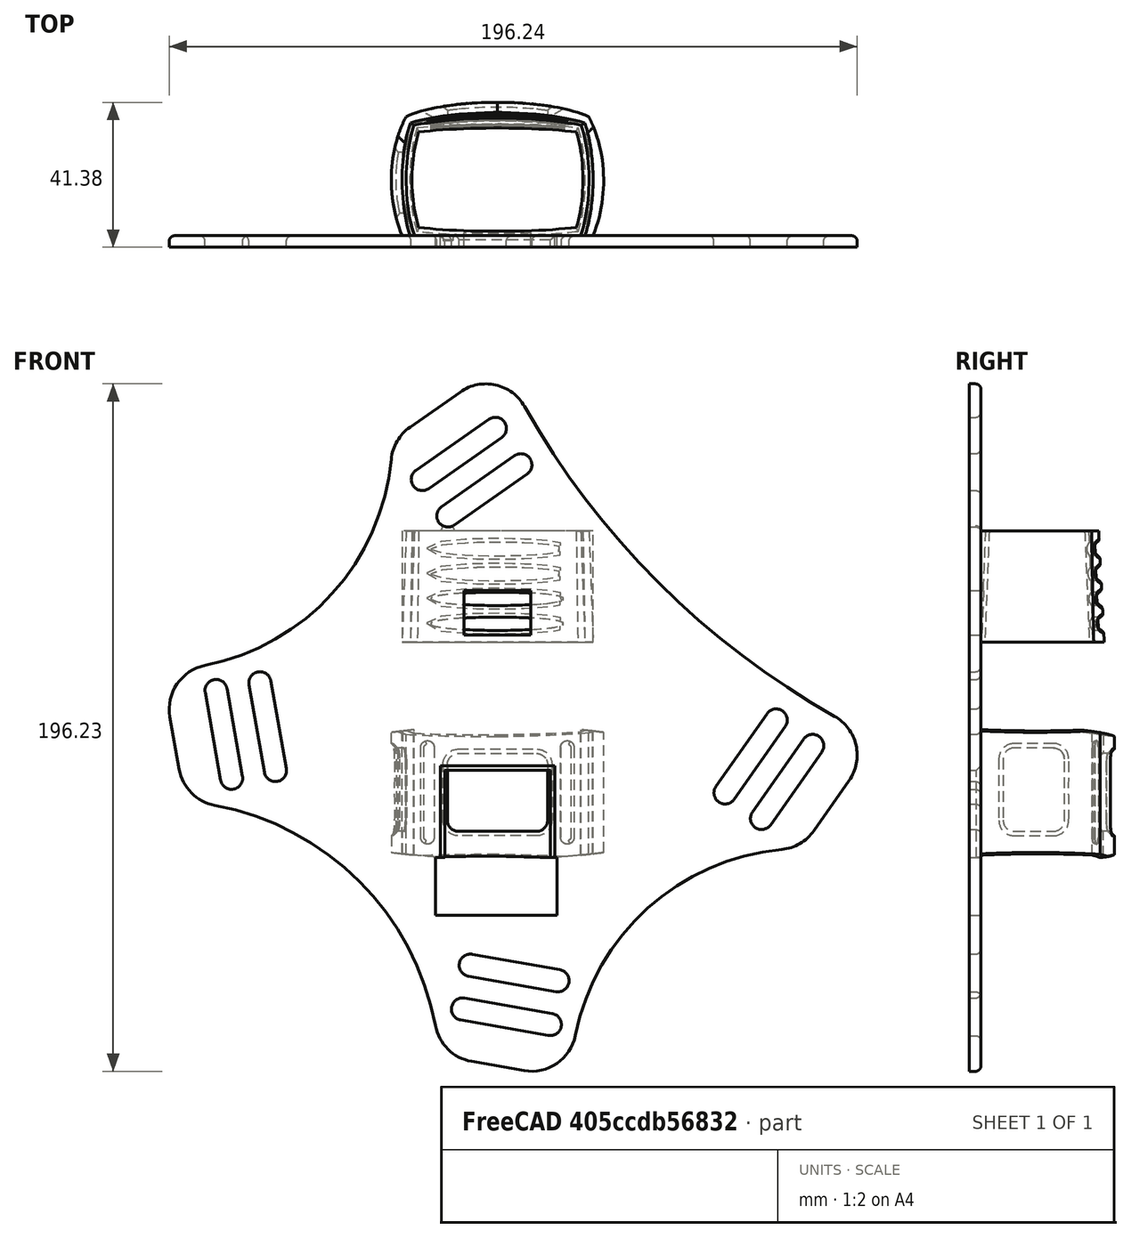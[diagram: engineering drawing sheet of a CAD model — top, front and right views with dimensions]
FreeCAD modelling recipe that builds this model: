
FCSTD DOCUMENT  (FreeCAD 0.20R29177 (Git))
Label: v2_1
License: All rights reserved
LicenseURL: http://en.wikipedia.org/wiki/All_rights_reserved
objects: Sketcher::SketchObject×23, PartDesign::Pocket×11, PartDesign::Pad×6, PartDesign::Fillet×3, PartDesign::Plane×2, PartDesign::SubtractiveLoft×2, PartDesign::Chamfer×1, PartDesign::Body×1
note: 72 computed .brp shape members not serialized (recipe doc carries the construction recipe); baked Part::Feature solids carry a one-line shape summary decoded from their .brp

FEATURE [Sketcher::SketchObject] Sketch
  FullyConstrained = false
  MapMode = 5
  Support = -> [XY_Plane]
  sketch-geometry (33):
    g0: ArcOfEllipse CenterX=0 CenterY=14.8987 CenterZ=0 NormalX=0 NormalY=0 NormalZ=1 MajorRadius=33.1985 MinorRadius=27.0767 AngleXU=-1.48295 StartAngle=4.10821 EndAngle=5.10673
    g1: ArcOfEllipse CenterX=0 CenterY=14.8987 CenterZ=0 NormalX=0 NormalY=0 NormalZ=1 MajorRadius=33.1985 MinorRadius=27.0767 AngleXU=-1.64554 StartAngle=1.16593 EndAngle=2.16406
    g2: ArcOfEllipse CenterX=0.00426746 CenterY=30.0382 CenterZ=0 NormalX=0 NormalY=0 NormalZ=1 MajorRadius=25.3994 MinorRadius=4.86502 AngleXU=3.14061 StartAngle=3.50205 EndAngle=5.93299
    g3: LineSegment StartX=-23.7833 StartY=0 StartZ=0 EndX=23.8417 EndY=0 EndZ=0
    g4: LineSegment StartX=-23.8519 StartY=31.7308 StartZ=0 EndX=23.7731 EndY=31.7308 EndZ=0
    g5: GeomPoint X=-26.9875 Y=12.7 Z=0
    g6: LineSegment StartX=-26.9875 StartY=12.7 StartZ=0 EndX=26.9875 EndY=12.7 EndZ=0
    g7: LineSegment StartX=0 StartY=0 StartZ=0 EndX=26.9875 EndY=12.7 EndZ=0
    g8: LineSegment StartX=0 StartY=0 StartZ=0 EndX=-26.9875 EndY=12.7 EndZ=0
    g9: LineSegment StartX=-26.9875 StartY=0 StartZ=0 EndX=-26.9875 EndY=12.7 EndZ=0
    g10: ArcOfEllipse CenterX=0.00426746 CenterY=30.0382 CenterZ=0 NormalX=0 NormalY=0 NormalZ=1 MajorRadius=29.8873 MinorRadius=8.04002 AngleXU=3.14073 StartAngle=3.65661 EndAngle=5.7746
    g11: LineSegment StartX=23.7731 StartY=31.7308 StartZ=0 EndX=26.0182 EndY=33.9758 EndZ=0
    g12: LineSegment StartX=-23.8519 StartY=31.7308 StartZ=0 EndX=-26.097 EndY=33.9758 EndZ=0
    g13: GeomPoint X=0 Y=34.9033 Z=0
    g14: LineSegment StartX=0 StartY=34.9033 StartZ=0 EndX=0 EndY=38.0783 EndZ=0
    g15: LineSegment StartX=26.9875 StartY=12.7 StartZ=0 EndX=30.1526 EndY=12.4491 EndZ=0
    g16: GeomPoint X=26.9875 Y=12.7 Z=0
    g17: LineSegment StartX=23.8417 StartY=0 StartZ=0 EndX=26.7524 EndY=-1.26846 EndZ=0
    g18: GeomPoint X=23.8417 Y=6e-16 Z=0
    g19: ArcOfEllipse CenterX=2.35624 CenterY=14.2309 CenterZ=0 NormalX=0 NormalY=0 NormalZ=1 MajorRadius=34.768 MinorRadius=27.8462 AngleXU=1.46882 StartAngle=4.37163 EndAngle=5.39941
    g20: LineSegment StartX=-26.9875 StartY=12.7 StartZ=0 EndX=-30.1514 EndY=12.4352 EndZ=0
    g21: LineSegment StartX=-23.7833 StartY=0 StartZ=0 EndX=-26.6887 EndY=-1.28025 EndZ=0
    g22: GeomPoint X=-23.7833 Y=-5.07e-13 Z=0
    g23: GeomPoint X=-26.9875 Y=12.7 Z=0
    g24: ArcOfEllipse CenterX=-2.35136 CenterY=14.2309 CenterZ=0 NormalX=0 NormalY=0 NormalZ=1 MajorRadius=34.768 MinorRadius=27.8462 AngleXU=1.68398 StartAngle=0.874461 EndAngle=1.90273
    g25: GeomPoint X=0 Y=-6.45413 Z=0
    g26: LineSegment StartX=2.35624 StartY=14.2309 StartZ=0 EndX=-2.35136 EndY=14.2309 EndZ=0
    g27: GeomPoint X=27.2821 Y=0 Z=0
    g28: GeomPoint X=-27.2294 Y=0 Z=0
    g29: LineSegment StartX=27.2821 StartY=0 StartZ=0 EndX=27.2821 EndY=-3.175 EndZ=0
    g30: LineSegment StartX=27.2821 StartY=-3.175 StartZ=0 EndX=-27.2294 EndY=-3.175 EndZ=0
    g31: LineSegment StartX=-27.2294 StartY=-3.175 StartZ=0 EndX=-27.2294 EndY=0 EndZ=0
    g32: LineSegment StartX=-23.7833 StartY=0 StartZ=0 EndX=23.8417 EndY=0 EndZ=0
  constraints (91):
    c: PointOnObject(g0,g-1)
    c: PointOnObject(g1,g-1)
    c: DistanceX(g0,g1) = 47.625
    c: Coincident(g1,g2)
    c: Coincident(g3,g0)
    c: Coincident(g3,g1)
    c: Block(g2)
    c: Coincident(g0,g2)
    c: Coincident(g4,g0)
    c: Coincident(g4,g1)
    c: Horizontal(g4)
    c: DistanceX(g4,g4) = 47.625
    c: PointOnObject(g5,g0)
    c: Coincident(g6,g5)
    c: Horizontal(g6)
    c: DistanceX(g6,g6) = 53.975
    c: PointOnObject(g6,g1)
    c: Coincident(g7,g-1)
    c: Coincident(g7,g6)
    c: Coincident(g8,g7)
    c: Coincident(g8,g5)
    c: Equal(g0,g1)
    c: PointOnObject(g9,g-1)
    c: Vertical(g9)
    c: Coincident(g9,g5)
    c: DistanceY(g9,g9) = 12.7
    c: Equal(g8,g7)
    c: PointOnObject(g1,g-2)
    c: Coincident(g0,g1)
    c: Coincident(g10,g2)
    c: Coincident(g11,g1)
    c: Coincident(g12,g0)
    c: Angle(g11) = 0.785398
    c: Perpendicular(g12,g11)
    c: Distance(g11) = 3.175
    c: Equal(g12,g11)
    c: Coincident(g10,g11)
    c: PointOnObject(g13,g2)
    c: PointOnObject(g13,g-2)
    c: Coincident(g14,g13)
    c: PointOnObject(g14,g10)
    c: PointOnObject(g14,g-2)
    c: DistanceY(g14,g14) = 3.175
    c: Coincident(g10,g12)
    c: Coincident(g15,g6)
    c: PointOnObject(g16,g1)
    c: PointOnObject(g16,g15)
    c: Perpendicular(g1,g15,g16) = 4.71239
    c: Distance(g15) = 3.175
    c: Coincident(g17,g1)
    c: PointOnObject(g18,g1)
    c: PointOnObject(g18,g17)
    c: Perpendicular(g1,g17,g18) = 4.71239
    c: Distance(g17) = 3.175
    c: Coincident(g19,g10)
    c: Coincident(g20,g5)
    c: Coincident(g21,g0)
    c: PointOnObject(g22,g0)
    c: PointOnObject(g22,g21)
    c: Perpendicular(g0,g21,g22) = 4.71239
    c: PointOnObject(g23,g0)
    c: PointOnObject(g23,g20)
    c: Perpendicular(g0,g20,g23) = 4.71239
    c: Equal(g20,g21)
    c: Equal(g21,g17)
    c: InternalAlignment(g25,g24)
    c: PointOnObject(g20,g24)
    c: Coincident(g24,g10)
    c: PointOnObject(g15,g19)
    c: Equal(g19,g24)
    c: Coincident(g26,g19)
    c: Coincident(g26,g24)
    c: Horizontal(g26)
    c: PointOnObject(g25,g-2)
    c: PointOnObject(g27,g-1)
    c: PointOnObject(g27,g19)
    c: PointOnObject(g28,g24)
    c: PointOnObject(g28,g-1)
    c: Coincident(g29,g30)
    c: Coincident(g30,g31)
    c: Horizontal(g30)
    c: Vertical(g29)
    c: Vertical(g31)
    c: PointOnObject(g27,g29)
    c: DistanceY(g29,g29) = 3.175
    c: PointOnObject(g24,g31)
    c: PointOnObject(g19,g29)
    c: Block(g24)
    c: Coincident(g32,g0)
    c: PointOnObject(g32,g17)
    c: Horizontal(g32)
FEATURE [PartDesign::Pad] Pad
  Direction = (0,0,1)
  Length = 38.1
  Length2 = 9.906
  Profile = -> Sketch
  ReferenceAxis = -> Sketch [N_Axis]
  Type = 0
FEATURE [Sketcher::SketchObject] Sketch001
  FullyConstrained = true
  MapMode = 5
  Placement = pos=(0,0,0) rot=(1,0,0;1.5708rad)
  Support = -> [XZ_Plane]
FEATURE [PartDesign::Plane] DatumPlane
  AttachmentOffset = pos=(25.4,25.4,50.8) rot=(0,0,1;0rad)
  Length = 235.383
  MapMode = 5
  Placement = pos=(-25.4,50.8,25.4) rot=(0,0.707107,0.707107;3.14159rad)
  ResizeMode = 0
  Support = -> [Pad]
  Width = 235.383
FEATURE [Sketcher::SketchObject] Sketch002
  ExternalGeometry = -> [Pad]
  FullyConstrained = true
  MapMode = 5
  Placement = pos=(-25.4,50.8,25.4) rot=(0,0.707107,0.707107;3.14159rad)
  Support = -> [DatumPlane]
  sketch-geometry (15):
    g0: LineSegment StartX=-36.5168 StartY=4.7625 StartZ=0 EndX=-14.2918 EndY=4.7625 EndZ=0
    g1: LineSegment StartX=-11.1168 StartY=1.5875 StartZ=0 EndX=-11.1168 EndY=-14.2875 EndZ=0
    g2: LineSegment StartX=-14.2918 StartY=-17.4625 StartZ=0 EndX=-36.5168 EndY=-17.4625 EndZ=0
    g3: LineSegment StartX=-39.6918 StartY=-14.2875 StartZ=0 EndX=-39.6918 EndY=1.5875 EndZ=0
    g4: LineSegment StartX=-55.2916 StartY=-25.4 StartZ=0 EndX=-39.6918 EndY=-17.4625 EndZ=0
    g5: LineSegment StartX=4.48307 StartY=-25.4 StartZ=0 EndX=-11.1168 EndY=-17.4625 EndZ=0
    g6: LineSegment StartX=4.48307 StartY=12.7 StartZ=0 EndX=-11.1168 EndY=4.7625 EndZ=0
    g7: ArcOfCircle CenterX=-36.5168 CenterY=1.5875 CenterZ=0 NormalX=0 NormalY=0 NormalZ=1 AngleXU=0 Radius=3.175 StartAngle=1.5708 EndAngle=3.14159
    g8: GeomPoint X=-39.6918 Y=4.7625 Z=0
    g9: ArcOfCircle CenterX=-36.5168 CenterY=-14.2875 CenterZ=0 NormalX=0 NormalY=0 NormalZ=1 AngleXU=0 Radius=3.175 StartAngle=3.14159 EndAngle=4.71239
    g10: GeomPoint X=-39.6918 Y=-17.4625 Z=0
    g11: ArcOfCircle CenterX=-14.2918 CenterY=-14.2875 CenterZ=0 NormalX=0 NormalY=0 NormalZ=1 AngleXU=0 Radius=3.175 StartAngle=4.71239 EndAngle=6.28319
    g12: GeomPoint X=-11.1168 Y=-17.4625 Z=0
    g13: ArcOfCircle CenterX=-14.2918 CenterY=1.5875 CenterZ=0 NormalX=0 NormalY=0 NormalZ=1 AngleXU=0 Radius=3.175 StartAngle=2.52e-14 EndAngle=1.5708
    g14: GeomPoint X=-11.1168 Y=4.7625 Z=0
  constraints (34):
    c: Horizontal(g0)
    c: Horizontal(g2)
    c: Vertical(g1)
    c: Vertical(g3)
    c: DistanceX(g8,g14) = 28.575
    c: DistanceY(g12,g14) = 22.225
    c: Coincident(g4,g-3)
    c: Coincident(g4,g10)
    c: Coincident(g5,g-3)
    c: Coincident(g5,g12)
    c: Coincident(g6,g-4)
    c: Coincident(g6,g14)
    c: Equal(g6,g5)
    c: Equal(g5,g4)
    c: PointOnObject(g8,g0)
    c: PointOnObject(g8,g3)
    c: Tangent(g0,g7) = 1.5708
    c: Tangent(g3,g7) = 1.5708
    c: PointOnObject(g10,g2)
    c: PointOnObject(g10,g3)
    c: Tangent(g2,g9) = 1.5708
    c: Tangent(g3,g9) = 1.5708
    c: PointOnObject(g12,g2)
    c: PointOnObject(g12,g1)
    c: Tangent(g2,g11) = 1.5708
    c: Tangent(g1,g11) = 1.5708
    c: PointOnObject(g14,g1)
    c: PointOnObject(g14,g0)
    c: Tangent(g1,g13) = 1.5708
    c: Tangent(g0,g13) = 1.5708
    c: Equal(g7,g9)
    c: Equal(g9,g11)
    c: Equal(g11,g13)
    c: Radius(g13) = 3.175
FEATURE [PartDesign::Pocket] Pocket
  BaseFeature = -> Pad
  Direction = (0,-1,2e-16)
  Length = 0
  Length2 = 5.08
  Profile = -> Sketch002
  ReferenceAxis = -> Sketch002 [N_Axis]
  Type = 3
  UpToFace = -> Pad [Face8]
FEATURE [Sketcher::SketchObject] Sketch003
  FullyConstrained = true
  MapMode = 5
  Placement = pos=(-25.4,50.8,25.4) rot=(0,0.707107,0.707107;3.14159rad)
  Support = -> [DatumPlane]
FEATURE [Sketcher::SketchObject] Sketch004
  ExternalGeometry = -> [Pocket]
  FullyConstrained = true
  MapMode = 5
  Placement = pos=(0,0,0) rot=(0.57735,0.57735,0.57735;2.0944rad)
  Support = -> [YZ_Plane]
  sketch-geometry (17):
    g0: LineSegment StartX=9.525 StartY=31.75 StartZ=0 EndX=20.6375 EndY=31.75 EndZ=0
    g1: LineSegment StartX=23.8125 StartY=28.575 StartZ=0 EndX=23.8125 EndY=11.1125 EndZ=0
    g2: LineSegment StartX=20.6375 StartY=7.9375 StartZ=0 EndX=9.525 EndY=7.9375 EndZ=0
    g3: LineSegment StartX=6.35 StartY=11.1125 StartZ=0 EndX=6.35 EndY=28.575 EndZ=0
    g4: ArcOfCircle CenterX=9.525 CenterY=28.575 CenterZ=0 NormalX=0 NormalY=0 NormalZ=1 AngleXU=0 Radius=3.175 StartAngle=1.5708 EndAngle=3.14159
    g5: GeomPoint X=6.35 Y=31.75 Z=0
    g6: ArcOfCircle CenterX=20.6375 CenterY=28.575 CenterZ=0 NormalX=0 NormalY=0 NormalZ=1 AngleXU=0 Radius=3.175 StartAngle=2e-16 EndAngle=1.5708
    g7: GeomPoint X=23.8125 Y=31.75 Z=0
    g8: ArcOfCircle CenterX=20.6375 CenterY=11.1125 CenterZ=0 NormalX=0 NormalY=0 NormalZ=1 AngleXU=0 Radius=3.175 StartAngle=4.71239 EndAngle=6.28319
    g9: GeomPoint X=23.8125 Y=7.9375 Z=0
    g10: ArcOfCircle CenterX=9.525 CenterY=11.1125 CenterZ=0 NormalX=0 NormalY=0 NormalZ=1 AngleXU=0 Radius=3.175 StartAngle=3.14159 EndAngle=4.71239
    g11: GeomPoint X=6.35 Y=7.9375 Z=0
    g12: LineSegment StartX=6.35 StartY=28.575 StartZ=0 EndX=23.8125 EndY=28.575 EndZ=0
    g13: LineSegment StartX=9.525 StartY=31.75 StartZ=0 EndX=9.525 EndY=7.9375 EndZ=0
    g14: LineSegment StartX=6.35 StartY=28.575 StartZ=0 EndX=-3.175 EndY=28.575 EndZ=0
    g15: LineSegment StartX=-3.175 StartY=38.1 StartZ=0 EndX=31.7308 EndY=38.1 EndZ=0
    g16: LineSegment StartX=9.525 StartY=31.75 StartZ=0 EndX=9.525 EndY=38.1 EndZ=0
  constraints (40):
    c: Horizontal(g0)
    c: Horizontal(g2)
    c: Vertical(g1)
    c: Vertical(g3)
    c: PointOnObject(g5,g0)
    c: PointOnObject(g5,g3)
    c: Tangent(g0,g4) = 1.5708
    c: Tangent(g3,g4) = 1.5708
    c: PointOnObject(g7,g0)
    c: PointOnObject(g7,g1)
    c: Tangent(g0,g6) = 1.5708
    c: Tangent(g1,g6) = 1.5708
    c: PointOnObject(g9,g1)
    c: PointOnObject(g9,g2)
    c: Tangent(g1,g8) = 1.5708
    c: Tangent(g2,g8) = 1.5708
    c: PointOnObject(g11,g2)
    c: PointOnObject(g11,g3)
    c: Tangent(g2,g10) = 1.5708
    c: Tangent(g3,g10) = 1.5708
    c: Equal(g4,g6)
    c: Equal(g6,g8)
    c: Equal(g8,g10)
    c: Radius(g10) = 3.175
    c: Coincident(g12,g3)
    c: DistanceX(g12,g12) = 17.4625
    c: Coincident(g12,g1)
    c: Coincident(g13,g0)
    c: Coincident(g13,g2)
    c: DistanceY(g13,g13) = 23.8125
    c: Coincident(g14,g3)
    c: PointOnObject(g14,g-3)
    c: Horizontal(g14)
    c: DistanceX(g14,g14) = 9.525
    c: Coincident(g15,g-3)
    c: Coincident(g15,g-4)
    c: Coincident(g16,g0)
    c: PointOnObject(g16,g15)
    c: Vertical(g16)
    c: DistanceY(g16,g16) = 6.35
FEATURE [PartDesign::Pocket] Pocket001
  BaseFeature = -> Pocket
  Direction = (-1,2e-16,-3e-16)
  Length = 5.08
  Length2 = 5.08
  Profile = -> Sketch004
  ReferenceAxis = -> Sketch004 [N_Axis]
  Type = 1
FEATURE [Sketcher::SketchObject] Sketch005
  ExternalGeometry = -> [Pocket001]
  FullyConstrained = true
  MapMode = 5
  Placement = pos=(-25.4,50.8,25.4) rot=(0,0.707107,0.707107;3.14159rad)
  Support = -> [DatumPlane]
  sketch-geometry (11):
    g0: Ellipse CenterX=-25.4043 CenterY=-6.35 CenterZ=0 NormalX=0 NormalY=0 NormalZ=1 MajorRadius=69.5483 MinorRadius=19.05 AngleXU=-1e-16
    g1: LineSegment StartX=44.144 StartY=-6.35 StartZ=0 EndX=-94.9526 EndY=-6.35 EndZ=0
    g2: LineSegment StartX=-25.4043 StartY=12.7 StartZ=0 EndX=-25.4043 EndY=-25.4 EndZ=0
    g3: GeomPoint X=41.4842 Y=-6.35 Z=0
    g4: GeomPoint X=-92.2927 Y=-6.35 Z=0
    g5: LineSegment StartX=-55.2916 StartY=12.7 StartZ=0 EndX=-25.4043 EndY=-6.35 EndZ=0
    g6: LineSegment StartX=-25.4043 StartY=-6.35 StartZ=0 EndX=4.48307 EndY=12.7 EndZ=0
    g7: LineSegment StartX=-111.897 StartY=37.229 StartZ=0 EndX=59.9655 EndY=37.229 EndZ=0
    g8: LineSegment StartX=59.9655 StartY=37.229 StartZ=0 EndX=59.9655 EndY=-34.3386 EndZ=0
    g9: LineSegment StartX=59.9655 StartY=-34.3386 StartZ=0 EndX=-111.897 EndY=-34.3386 EndZ=0
    g10: LineSegment StartX=-111.897 StartY=-34.3386 StartZ=0 EndX=-111.897 EndY=37.229 EndZ=0
  constraints (20):
    c: InternalAlignment(g1-g4 -> g0) x4
    c: Tangent(g0,g-3)
    c: Vertical(g2)
    c: PointOnObject(g2,g-4)
    c: Coincident(g5,g-3)
    c: Coincident(g5,g0)
    c: Coincident(g6,g0)
    c: Coincident(g6,g-3)
    c: Equal(g6,g5)
    c: Coincident(g7,g8)
    c: Coincident(g8,g9)
    c: Coincident(g9,g10)
    c: Coincident(g10,g7)
    c: Horizontal(g7)
    c: Horizontal(g9)
    c: Vertical(g8)
    c: Vertical(g10)
    c: Block(g0)
    c: Block(g9)
    c: Block(g7)
FEATURE [PartDesign::Pocket] Pocket002
  BaseFeature = -> Pocket001
  Direction = (0,-1,2e-16)
  Length = 0
  Length2 = 5.08
  Profile = -> Sketch005
  ReferenceAxis = -> Sketch005 [N_Axis]
  Type = 3
  UpToFace = -> Pocket001 [Face16]
FEATURE [Sketcher::SketchObject] Sketch006
  FullyConstrained = true
  MapMode = 5
  Placement = pos=(0,0,0) rot=(0.57735,0.57735,0.57735;2.0944rad)
  Support = -> [YZ_Plane]
  sketch-geometry (7):
    g0: Ellipse CenterX=-43.899 CenterY=18.1751 CenterZ=0 NormalX=0 NormalY=0 NormalZ=1 MajorRadius=123.401 MinorRadius=22.5272 AngleXU=0
    g1: GeomPoint X=77.4281 Y=18.1751 Z=0
    g2: GeomPoint X=-165.226 Y=18.1751 Z=0
    g3: LineSegment StartX=-223.185 StartY=118.003 StartZ=0 EndX=167.895 EndY=118.003 EndZ=0
    g4: LineSegment StartX=167.895 StartY=118.003 StartZ=0 EndX=167.895 EndY=-87.3007 EndZ=0
    g5: LineSegment StartX=167.895 StartY=-87.3007 StartZ=0 EndX=-223.185 EndY=-87.3007 EndZ=0
    g6: LineSegment StartX=-223.185 StartY=-87.3007 StartZ=0 EndX=-223.185 EndY=118.003 EndZ=0
  constraints (13):
    c: InternalAlignment(g1,g0)
    c: InternalAlignment(g2,g0)
    c: Coincident(g3,g4)
    c: Coincident(g4,g5)
    c: Coincident(g5,g6)
    c: Coincident(g6,g3)
    c: Horizontal(g3)
    c: Horizontal(g5)
    c: Vertical(g4)
    c: Vertical(g6)
    c: Block(g0)
    c: Block(g3)
    c: Block(g4)
FEATURE [PartDesign::Pocket] Pocket003
  BaseFeature = -> Pocket002
  Direction = (-1,2e-16,-3e-16)
  Length = 233.68
  Length2 = 157.48
  Profile = -> Sketch006
  ReferenceAxis = -> Sketch006 [N_Axis]
  TaperAngle2 = 1
  Type = 4
FEATURE [Sketcher::SketchObject] Sketch007
  ExternalGeometry = -> [Pocket003]
  FullyConstrained = true
  MapMode = 5
  Placement = pos=(0,-3.175,0) rot=(1,0,0;1.5708rad)
  sketch-geometry (6):
    g0: LineSegment StartX=-15.077 StartY=0 StartZ=0 EndX=15.0855 EndY=0 EndZ=0
    g1: LineSegment StartX=15.0855 StartY=0 StartZ=0 EndX=15.0855 EndY=25.4 EndZ=0
    g2: LineSegment StartX=15.0855 StartY=25.4 StartZ=0 EndX=-15.077 EndY=25.4 EndZ=0
    g3: LineSegment StartX=-15.077 StartY=25.4 StartZ=0 EndX=-15.077 EndY=0 EndZ=0
    g4: LineSegment StartX=-11.1082 StartY=30.1625 StartZ=0 EndX=-15.077 EndY=25.4 EndZ=0
    g5: LineSegment StartX=11.1168 StartY=30.1625 StartZ=0 EndX=15.0855 EndY=25.4 EndZ=0
  constraints (15):
    c: Coincident(g0,g1)
    c: Coincident(g1,g2)
    c: Coincident(g2,g3)
    c: Coincident(g3,g0)
    c: Horizontal(g2)
    c: Vertical(g1)
    c: Vertical(g3)
    c: DistanceX(g2,g2) = 30.1625
    c: Coincident(g4,g2)
    c: Coincident(g5,g1)
    c: Equal(g4,g5)
    c: DistanceY(g1,g1) = 25.4
    c: Tangent(g-1,g0)
    c: Coincident(g5,g-3)
    c: Coincident(g4,g-4)
FEATURE [PartDesign::Pocket] Pocket004
  BaseFeature = -> Pocket003
  Direction = (0,1,-2e-16)
  Length = 5.08
  Length2 = 5.08
  Profile = -> Sketch007
  ReferenceAxis = -> Sketch007 [N_Axis]
  Type = 2
FEATURE [PartDesign::Chamfer] Chamfer
  Angle = 45
  Base = -> Pocket004 [Edge11,Edge89,Edge88,Edge39,Edge87]
  BaseFeature = -> Pocket004
  ChamferType = 0
  FlipDirection = false
  Size = 1.27
  Size2 = 1
  SupportTransform = false
  UseAllEdges = false
FEATURE [PartDesign::Plane] DatumPlane001
  Length = 235.449
  MapMode = 13
  Placement = pos=(3.70843,34.4094,22.7542) rot=(0.000335,0.707107,0.707107;3.14092rad)
  ResizeMode = 0
  Support = -> [Chamfer]
  Width = 235.389
FEATURE [Sketcher::SketchObject] Sketch008
  ExternalGeometry = -> [Chamfer]
  FullyConstrained = true
  MapMode = 5
  Placement = pos=(3.70843,34.4094,22.7542) rot=(0.000335,0.707107,0.707107;3.14092rad)
  Support = -> [DatumPlane001]
  sketch-geometry (14):
    g0: ArcOfCircle CenterX=23.684 CenterY=9.16871 CenterZ=0 NormalX=0 NormalY=0 NormalZ=1 AngleXU=0 Radius=1.905 StartAngle=0 EndAngle=3.14159
    g1: ArcOfCircle CenterX=23.684 CenterY=-16.5768 CenterZ=0 NormalX=0 NormalY=0 NormalZ=1 AngleXU=0 Radius=1.905 StartAngle=3.14159 EndAngle=6.28319
    g2: LineSegment StartX=21.779 StartY=9.16871 StartZ=0 EndX=21.779 EndY=-16.5768 EndZ=0
    g3: LineSegment StartX=25.589 StartY=-16.5768 StartZ=0 EndX=25.589 EndY=9.16871 EndZ=0
    g4: ArcOfCircle CenterX=-16.2188 CenterY=-16.5768 CenterZ=0 NormalX=0 NormalY=0 NormalZ=1 AngleXU=0 Radius=1.905 StartAngle=3.14159 EndAngle=6.28319
    g5: ArcOfCircle CenterX=-16.2188 CenterY=9.16871 CenterZ=0 NormalX=0 NormalY=0 NormalZ=1 AngleXU=0 Radius=1.905 StartAngle=2e-16 EndAngle=3.14159
    g6: LineSegment StartX=-14.3138 StartY=-16.5768 StartZ=0 EndX=-14.3138 EndY=9.16871 EndZ=0
    g7: LineSegment StartX=-18.1238 StartY=9.16871 StartZ=0 EndX=-18.1238 EndY=-16.5768 EndZ=0
    g8: LineSegment StartX=-16.2188 StartY=-16.5768 StartZ=0 EndX=23.684 EndY=-16.5768 EndZ=0
    g9: LineSegment StartX=19.2484 StartY=-11.6887 StartZ=0 EndX=23.684 EndY=-16.5768 EndZ=0
    g10: LineSegment StartX=19.2484 StartY=4.28068 StartZ=0 EndX=23.684 EndY=9.16871 EndZ=0
    g11: LineSegment StartX=-11.8358 StartY=4.23333 StartZ=0 EndX=-16.2188 EndY=9.16871 EndZ=0
    g12: LineSegment StartX=-11.835 StartY=-11.689 StartZ=0 EndX=-14.3138 EndY=-11.689 EndZ=0
    g13: LineSegment StartX=-18.1238 StartY=-16.5768 StartZ=0 EndX=-20.0672 EndY=-15.0381 EndZ=0
  constraints (33):
    c: Tangent(g0,g2) = -1.5708
    c: Tangent(g2,g1) = -1.5708
    c: Tangent(g1,g3) = -1.5708
    c: Tangent(g3,g0) = -1.5708
    c: Equal(g0,g1)
    c: Vertical(g2)
    c: Tangent(g4,g6) = -1.5708
    c: Tangent(g6,g5) = -1.5708
    c: Tangent(g5,g7) = -1.5708
    c: Tangent(g7,g4) = -1.5708
    c: Equal(g4,g5)
    c: Vertical(g6)
    c: Equal(g5,g0)
    c: Coincident(g8,g4)
    c: Coincident(g8,g1)
    c: Horizontal(g8)
    c: Equal(g2,g6)
    c: Coincident(g9,g-5)
    c: Coincident(g9,g1)
    c: Coincident(g10,g-6)
    c: Coincident(g10,g0)
    c: Equal(g10,g9)
    c: Coincident(g11,g-3)
    c: Coincident(g11,g5)
    c: Equal(g11,g10)
    c: Coincident(g12,g-4)
    c: PointOnObject(g12,g6)
    c: Horizontal(g12)
    c: Coincident(g13,g4)
    c: PointOnObject(g13,g-7)
    c: Equal(g12,g13)
    c: Radius(g4) = 1.905
    c: Block(g1)
FEATURE [PartDesign::Pad] Pad001
  BaseFeature = -> Chamfer
  Direction = (0.000946446,1,0)
  Length = 2.54
  Length2 = 9.906
  Profile = -> Sketch008
  ReferenceAxis = -> Sketch008 [N_Axis]
  Reversed = true
  Type = 0
FEATURE [PartDesign::Fillet] Fillet
  Base = -> Pad001 [Edge161,Edge167]
  BaseFeature = -> Pad001
  Radius = 0.999998
  SupportTransform = false
  UseAllEdges = false
FEATURE [Sketcher::SketchObject] Sketch009
  ExternalGeometry = -> [Fillet]
  FullyConstrained = false
  MapMode = 5
  Placement = pos=(0,-3.175,0) rot=(1,0,0;1.5708rad)
  Support = -> [Fillet]
  sketch-geometry (8):
    g0: LineSegment StartX=-27.2294 StartY=36.5788 StartZ=0 EndX=27.2821 EndY=36.5788 EndZ=0
    g1: LineSegment StartX=27.2821 StartY=36.5788 StartZ=0 EndX=27.2821 EndY=36.5736 EndZ=0
    g2: LineSegment StartX=27.2821 StartY=36.5736 StartZ=0 EndX=-27.2294 EndY=36.5736 EndZ=0
    g3: LineSegment StartX=-27.2294 StartY=36.5736 StartZ=0 EndX=-27.2294 EndY=36.5788 EndZ=0
    g4: LineSegment StartX=-27.2294 StartY=36.5788 StartZ=0 EndX=27.2821 EndY=36.5788 EndZ=0
    g5: LineSegment StartX=27.2821 StartY=36.5788 StartZ=0 EndX=27.2821 EndY=93.7288 EndZ=0
    g6: LineSegment StartX=27.2821 StartY=93.7288 StartZ=0 EndX=-27.2294 EndY=93.7288 EndZ=0
    g7: LineSegment StartX=-27.2294 StartY=93.7288 StartZ=0 EndX=-27.2294 EndY=36.5788 EndZ=0
  constraints (20):
    c: Coincident(g0,g1)
    c: Coincident(g1,g2)
    c: Coincident(g2,g3)
    c: Coincident(g3,g0)
    c: Horizontal(g0)
    c: Horizontal(g2)
    c: Vertical(g1)
    c: Vertical(g3)
    c: Coincident(g0,g-4)
    c: Coincident(g4,g5)
    c: Coincident(g5,g6)
    c: Coincident(g6,g7)
    c: Coincident(g7,g4)
    c: Horizontal(g6)
    c: Vertical(g5)
    c: Vertical(g7)
    c: Coincident(g4,g0)
    c: Coincident(g4,g0)
    c: PointOnObject(g-3,g5)
    c: DistanceY(g5,g5) = 57.15
FEATURE [PartDesign::Pad] Pad002
  BaseFeature = -> Fillet
  Direction = (0,-1,2e-16)
  Length = 9.906
  Length2 = 9.906
  Profile = -> Sketch009
  ReferenceAxis = -> Sketch009 [N_Axis]
  Type = 3
  UpToFace = -> Fillet [Face34]
FEATURE [Sketcher::SketchObject] Sketch010
  ExternalGeometry = -> [Pad002]
  FullyConstrained = true
  MapMode = 5
  Placement = pos=(0,-3.175,7e-16) rot=(1,0,0;1.5708rad)
  Support = -> [Pad002]
  sketch-geometry (5):
    g0: LineSegment StartX=-27.2294 StartY=93.7288 StartZ=0 EndX=27.2821 EndY=93.7288 EndZ=0
    g1: LineSegment StartX=27.2821 StartY=93.7288 StartZ=0 EndX=27.2821 EndY=61.9736 EndZ=0
    g2: LineSegment StartX=27.2821 StartY=61.9736 StartZ=0 EndX=-27.2294 EndY=61.9736 EndZ=0
    g3: LineSegment StartX=-27.2294 StartY=61.9736 StartZ=0 EndX=-27.2294 EndY=93.7288 EndZ=0
    g4: LineSegment StartX=27.2821 StartY=36.5736 StartZ=0 EndX=27.2821 EndY=61.9736 EndZ=0
  constraints (13):
    c: Coincident(g0,g1)
    c: Coincident(g1,g2)
    c: Coincident(g2,g3)
    c: Coincident(g3,g0)
    c: Horizontal(g0)
    c: Horizontal(g2)
    c: Vertical(g1)
    c: Vertical(g3)
    c: Coincident(g0,g-3)
    c: Coincident(g4,g-4)
    c: Coincident(g4,g1)
    c: Vertical(g4)
    c: DistanceY(g4,g4) = 25.4
FEATURE [PartDesign::Pad] Pad003
  BaseFeature = -> Pad002
  Direction = (0,-1,2e-16)
  Length = 41.529
  Length2 = 9.906
  Profile = -> Sketch010
  ReferenceAxis = -> Sketch010 [N_Axis]
  Reversed = true
  Type = 0
FEATURE [Sketcher::SketchObject] Sketch011
  ExternalGeometry = -> [Pad003]
  FullyConstrained = true
  MapMode = 5
  Placement = pos=(0,1.36e-14,61.9736) rot=(1,0,0;3.14159rad)
  Support = -> [Pad003]
  sketch-geometry (54):
    g0: LineSegment StartX=24.9184 StartY=2.08e-14 StartZ=0 EndX=-24.8656 EndY=2.08e-14 EndZ=0
    g1: LineSegment StartX=-24.8656 StartY=2.08e-14 StartZ=0 EndX=-24.8656 EndY=-32.004 EndZ=0
    g2: LineSegment StartX=-24.8656 StartY=-32.004 StartZ=0 EndX=24.9184 EndY=-32.004 EndZ=0
    g3: LineSegment StartX=24.9184 StartY=-32.004 StartZ=0 EndX=24.9184 EndY=2.13e-14 EndZ=0
    g4: LineSegment StartX=-24.8656 StartY=-32.004 StartZ=0 EndX=-27.2294 EndY=-32.004 EndZ=0
    g5: LineSegment StartX=24.9184 StartY=-32.004 StartZ=0 EndX=27.2821 EndY=-32.004 EndZ=0
    g6: Ellipse CenterX=0 CenterY=-27.305 CenterZ=0 NormalX=0 NormalY=0 NormalZ=1 MajorRadius=35.56 MinorRadius=4.699 AngleXU=0
    g7: LineSegment StartX=35.56 StartY=-27.305 StartZ=0 EndX=-35.56 EndY=-27.305 EndZ=0
    g8: LineSegment StartX=0 StartY=-22.606 StartZ=0 EndX=0 EndY=-32.004 EndZ=0
    g9: GeomPoint X=35.2482 Y=-27.305 Z=0
    g10: GeomPoint X=-35.2482 Y=-27.305 Z=0
    g11: GeomPoint X=0 Y=-32.004 Z=0
    g12: Ellipse CenterX=0 CenterY=-4.699 CenterZ=0 NormalX=0 NormalY=0 NormalZ=1 MajorRadius=35.56 MinorRadius=4.699 AngleXU=0
    g13: LineSegment StartX=35.56 StartY=-4.699 StartZ=0 EndX=-35.56 EndY=-4.699 EndZ=0
    g14: LineSegment StartX=0 StartY=0 StartZ=0 EndX=0 EndY=-9.398 EndZ=0
    g15: GeomPoint X=35.2482 Y=-4.699 Z=0
    g16: GeomPoint X=-35.2482 Y=-4.699 Z=0
    g17: LineSegment StartX=27.2821 StartY=-32.004 StartZ=0 EndX=24.9184 EndY=-16.002 EndZ=0
    g18: LineSegment StartX=27.2821 StartY=2.08e-14 StartZ=0 EndX=24.9184 EndY=-16.002 EndZ=0
    g19: LineSegment StartX=-27.2294 StartY=2.08e-14 StartZ=0 EndX=-24.8656 EndY=-16.002 EndZ=0
    g20: Ellipse CenterX=17.0444 CenterY=-16.002 CenterZ=0 NormalX=0 NormalY=0 NormalZ=1 MajorRadius=22.352 MinorRadius=7.874 AngleXU=1.5708
    g21: LineSegment StartX=17.0444 StartY=6.35 StartZ=0 EndX=17.0444 EndY=-38.354 EndZ=0
    g22: LineSegment StartX=9.17036 StartY=-16.002 StartZ=0 EndX=24.9184 EndY=-16.002 EndZ=0
    g23: GeomPoint X=17.0444 Y=4.91718 Z=0
    g24: GeomPoint X=17.0444 Y=-36.9212 Z=0
    g25: Ellipse CenterX=-16.9916 CenterY=-16.002 CenterZ=0 NormalX=0 NormalY=0 NormalZ=1 MajorRadius=22.352 MinorRadius=7.874 AngleXU=1.5708
    g26: LineSegment StartX=-16.9916 StartY=6.35 StartZ=0 EndX=-16.9916 EndY=-38.354 EndZ=0
    g27: LineSegment StartX=-24.8656 StartY=-16.002 StartZ=0 EndX=-9.11764 EndY=-16.002 EndZ=0
    g28: GeomPoint X=-16.9916 Y=4.91718 Z=0
    g29: GeomPoint X=-16.9916 Y=-36.9212 Z=0
    g30: GeomPoint X=22.9149 Y=-30.8983 Z=0
    g31: GeomPoint X=-22.8603 Y=-30.9043 Z=0
    g32: GeomPoint X=-22.8603 Y=-1.09966 Z=0
    g33: GeomPoint X=22.9149 Y=-1.10573 Z=0
    g34: ArcOfEllipse CenterX=0 CenterY=-27.305 CenterZ=0 NormalX=0 NormalY=0 NormalZ=1 MajorRadius=35.56 MinorRadius=4.699 AngleXU=-3.14159 StartAngle=0.872565 EndAngle=2.27104
    g35: LineSegment StartX=-35.56 StartY=-27.305 StartZ=0 EndX=35.56 EndY=-27.305 EndZ=0
    g36: LineSegment StartX=1.2e-15 StartY=-32.004 StartZ=0 EndX=-1.2e-15 EndY=-22.606 EndZ=0
    g37: GeomPoint X=-35.2482 Y=-27.305 Z=0
    g38: GeomPoint X=35.2482 Y=-27.305 Z=0
    g39: ArcOfEllipse CenterX=0 CenterY=-4.699 CenterZ=0 NormalX=0 NormalY=0 NormalZ=1 MajorRadius=35.56 MinorRadius=4.699 AngleXU=3.14159 StartAngle=4.01215 EndAngle=5.41062
    g40: LineSegment StartX=-35.56 StartY=-4.699 StartZ=0 EndX=35.56 EndY=-4.699 EndZ=0
    g41: LineSegment StartX=-1.2e-15 StartY=-9.398 StartZ=0 EndX=1.2e-15 EndY=-1.8e-15 EndZ=0
    g42: GeomPoint X=-35.2482 Y=-4.699 Z=0
    g43: GeomPoint X=35.2482 Y=-4.699 Z=0
    g44: ArcOfEllipse CenterX=17.0444 CenterY=-16.002 CenterZ=0 NormalX=0 NormalY=0 NormalZ=1 MajorRadius=22.352 MinorRadius=7.874 AngleXU=1.5708 StartAngle=3.98297 EndAngle=5.44181
    g45: LineSegment StartX=17.0444 StartY=6.35 StartZ=0 EndX=17.0444 EndY=-38.354 EndZ=0
    g46: LineSegment StartX=9.17036 StartY=-16.002 StartZ=0 EndX=24.9184 EndY=-16.002 EndZ=0
    g47: GeomPoint X=17.0444 Y=4.91718 Z=0
    g48: GeomPoint X=17.0444 Y=-36.9212 Z=0
    g49: ArcOfEllipse CenterX=-16.9916 CenterY=-16.002 CenterZ=0 NormalX=0 NormalY=0 NormalZ=1 MajorRadius=22.352 MinorRadius=7.874 AngleXU=1.5708 StartAngle=0.841008 EndAngle=2.30058
    g50: LineSegment StartX=-16.9916 StartY=6.35 StartZ=0 EndX=-16.9916 EndY=-38.354 EndZ=0
    g51: LineSegment StartX=-24.8656 StartY=-16.002 StartZ=0 EndX=-9.11764 EndY=-16.002 EndZ=0
    g52: GeomPoint X=-16.9916 Y=4.91718 Z=0
    g53: GeomPoint X=-16.9916 Y=-36.9212 Z=0
  constraints (75):
    c: Coincident(g0,g1)
    c: Coincident(g1,g2)
    c: Coincident(g2,g3)
    c: Coincident(g3,g0)
    c: Horizontal(g0)
    c: Horizontal(g2)
    c: Vertical(g1)
    c: Vertical(g3)
    c: PointOnObject(g0,g-7)
    c: DistanceX(g2,g2) = 49.784
    c: DistanceY(g1,g1) = 32.004
    c: Coincident(g4,g1)
    c: PointOnObject(g4,g-4)
    c: Coincident(g5,g2)
    c: PointOnObject(g5,g-8)
    c: Horizontal(g5)
    c: Horizontal(g4)
    c: Equal(g5,g4)
    c: InternalAlignment(g7-g10 -> g6) x4
    c: PointOnObject(g11,g2)
    c: PointOnObject(g11,g-2)
    c: Coincident(g8,g11)
    c: Horizontal(g7)
    c: DistanceY(g8,g8) = 9.398
    c: DistanceX(g7,g7) = 71.12
    c: InternalAlignment(g13-g16 -> g12) x4
    c: Coincident(g14,g-1)
    c: Horizontal(g13)
    c: Equal(g13,g7)
    c: Equal(g14,g8)
    c: Coincident(g17,g5)
    c: PointOnObject(g17,g3)
    c: Coincident(g18,g-8)
    c: Coincident(g18,g17)
    c: Coincident(g19,g-7)
    c: PointOnObject(g19,g1)
    c: Equal(g19,g18)
    c: Equal(g18,g17)
    c: InternalAlignment(g21-g24 -> g20) x4
    c: Tangent(g20,g-6)
    c: Vertical(g21)
    c: Coincident(g17,g22)
    c: DistanceX(g22,g22) = 15.748
    c: InternalAlignment(g26-g29 -> g25) x4
    c: Coincident(g27,g19)
    c: Horizontal(g27)
    c: Equal(g25,g20)
    c: PointOnObject(g30,g6)
    c: PointOnObject(g30,g20)
    c: PointOnObject(g31,g6)
    c: PointOnObject(g31,g25)
    c: PointOnObject(g32,g12)
    c: PointOnObject(g32,g25)
    c: PointOnObject(g33,g20)
    c: PointOnObject(g33,g12)
    c: InternalAlignment(g35-g38 -> g34) x4
    c: Coincident(g34,g6)
    c: PointOnObject(g7,g34)
    c: Coincident(g34,g31)
    c: Coincident(g34,g30)
    c: InternalAlignment(g40-g43 -> g39) x4
    c: Coincident(g39,g12)
    c: PointOnObject(g13,g39)
    c: Coincident(g39,g32)
    c: Coincident(g39,g33)
    c: InternalAlignment(g45-g48 -> g44) x4
    c: Coincident(g44,g20)
    c: PointOnObject(g22,g44)
    c: Coincident(g44,g39)
    c: Coincident(g44,g34)
    c: InternalAlignment(g50-g53 -> g49) x4
    c: Coincident(g49,g25)
    c: PointOnObject(g19,g49)
    c: Coincident(g49,g34)
    c: Coincident(g49,g39)
FEATURE [Sketcher::SketchObject] Sketch012
  ExternalGeometry = -> [Pad003,Sketch011]
  FullyConstrained = true
  MapMode = 5
  Placement = pos=(0,2.06e-14,93.7288) rot=(0,0,1;0rad)
  Support = -> [Pad003]
  sketch-geometry (51):
    g0: LineSegment StartX=-24.384 StartY=30.734 StartZ=0 EndX=24.384 EndY=30.734 EndZ=0
    g1: LineSegment StartX=24.384 StartY=30.734 StartZ=0 EndX=24.384 EndY=1.27 EndZ=0
    g2: LineSegment StartX=24.384 StartY=1.27 StartZ=0 EndX=-24.384 EndY=1.27 EndZ=0
    g3: LineSegment StartX=-24.384 StartY=1.27 StartZ=0 EndX=-24.384 EndY=30.734 EndZ=0
    g4: LineSegment StartX=-24.384 StartY=30.734 StartZ=0 EndX=0 EndY=27.305 EndZ=0
    g5: LineSegment StartX=0 StartY=27.305 StartZ=0 EndX=24.384 EndY=30.734 EndZ=0
    g6: LineSegment StartX=24.384 StartY=1.27 StartZ=0 EndX=0 EndY=4.699 EndZ=0
    g7: Ellipse CenterX=-16.9916 CenterY=16.002 CenterZ=0 NormalX=0 NormalY=0 NormalZ=1 MajorRadius=20.193 MinorRadius=7.39236 AngleXU=1.5708
    g8: LineSegment StartX=-16.9916 StartY=36.195 StartZ=0 EndX=-16.9916 EndY=-4.191 EndZ=0
    g9: LineSegment StartX=-24.384 StartY=16.002 StartZ=0 EndX=-9.59927 EndY=16.002 EndZ=0
    g10: GeomPoint X=-16.9916 Y=34.7932 Z=0
    g11: GeomPoint X=-16.9916 Y=-2.78923 Z=0
    g12: Ellipse CenterX=17.0444 CenterY=16.002 CenterZ=0 NormalX=0 NormalY=0 NormalZ=1 MajorRadius=20.193 MinorRadius=7.33964 AngleXU=1.5708
    g13: LineSegment StartX=17.0444 StartY=36.195 StartZ=0 EndX=17.0444 EndY=-4.191 EndZ=0
    g14: LineSegment StartX=9.70473 StartY=16.002 StartZ=0 EndX=24.384 EndY=16.002 EndZ=0
    g15: GeomPoint X=17.0444 Y=34.8139 Z=0
    g16: GeomPoint X=17.0444 Y=-2.80988 Z=0
    g17: Ellipse CenterX=0 CenterY=27.305 CenterZ=0 NormalX=0 NormalY=0 NormalZ=1 MajorRadius=30.4179 MinorRadius=3.429 AngleXU=0
    g18: LineSegment StartX=30.4179 StartY=27.305 StartZ=0 EndX=-30.4179 EndY=27.305 EndZ=0
    g19: LineSegment StartX=0 StartY=30.734 StartZ=0 EndX=0 EndY=23.876 EndZ=0
    g20: GeomPoint X=30.224 Y=27.305 Z=0
    g21: GeomPoint X=-30.224 Y=27.305 Z=0
    g22: Ellipse CenterX=0 CenterY=4.699 CenterZ=0 NormalX=0 NormalY=0 NormalZ=1 MajorRadius=30.4179 MinorRadius=3.429 AngleXU=0
    g23: LineSegment StartX=30.4179 StartY=4.699 StartZ=0 EndX=-30.4179 EndY=4.699 EndZ=0
    g24: LineSegment StartX=0 StartY=8.128 StartZ=0 EndX=0 EndY=1.27 EndZ=0
    g25: GeomPoint X=30.224 Y=4.699 Z=0
    g26: GeomPoint X=-30.224 Y=4.699 Z=0
    g27: GeomPoint X=-22.4504 Y=29.6186 Z=0
    g28: GeomPoint X=22.4648 Y=29.6169 Z=0
    g29: GeomPoint X=22.4648 Y=2.38713 Z=0
    g30: GeomPoint X=-22.4504 Y=2.38536 Z=0
    g31: ArcOfEllipse CenterX=0 CenterY=27.305 CenterZ=0 NormalX=0 NormalY=0 NormalZ=1 MajorRadius=30.4179 MinorRadius=3.429 AngleXU=-9.37e-14 StartAngle=0.739895 EndAngle=2.401
    g32: LineSegment StartX=30.4179 StartY=27.305 StartZ=0 EndX=-30.4179 EndY=27.305 EndZ=0
    g33: LineSegment StartX=3.212e-13 StartY=30.734 StartZ=0 EndX=-3.212e-13 EndY=23.876 EndZ=0
    g34: GeomPoint X=30.224 Y=27.305 Z=0
    g35: GeomPoint X=-30.224 Y=27.305 Z=0
    g36: ArcOfEllipse CenterX=17.0444 CenterY=16.002 CenterZ=0 NormalX=0 NormalY=0 NormalZ=1 MajorRadius=20.193 MinorRadius=7.33964 AngleXU=-1.5708 StartAngle=0.830865 EndAngle=2.31073
    g37: LineSegment StartX=17.0444 StartY=-4.191 StartZ=0 EndX=17.0444 EndY=36.195 EndZ=0
    g38: LineSegment StartX=24.384 StartY=16.002 StartZ=0 EndX=9.70473 EndY=16.002 EndZ=0
    g39: GeomPoint X=17.0444 Y=-2.80988 Z=0
    g40: GeomPoint X=17.0444 Y=34.8139 Z=0
    g41: ArcOfEllipse CenterX=0 CenterY=4.699 CenterZ=0 NormalX=0 NormalY=0 NormalZ=1 MajorRadius=30.4179 MinorRadius=3.429 AngleXU=2.115e-13 StartAngle=3.88219 EndAngle=5.54329
    g42: LineSegment StartX=30.4179 StartY=4.699 StartZ=0 EndX=-30.4179 EndY=4.699 EndZ=0
    g43: LineSegment StartX=-7.251e-13 StartY=8.128 StartZ=0 EndX=7.251e-13 EndY=1.27 EndZ=0
    g44: GeomPoint X=30.224 Y=4.699 Z=0
    g45: GeomPoint X=-30.224 Y=4.699 Z=0
    g46: ArcOfEllipse CenterX=-16.9916 CenterY=16.002 CenterZ=0 NormalX=0 NormalY=0 NormalZ=1 MajorRadius=20.193 MinorRadius=7.39236 AngleXU=1.5708 StartAngle=0.830746 EndAngle=2.31085
    g47: LineSegment StartX=-16.9916 StartY=36.195 StartZ=0 EndX=-16.9916 EndY=-4.191 EndZ=0
    g48: LineSegment StartX=-24.384 StartY=16.002 StartZ=0 EndX=-9.59927 EndY=16.002 EndZ=0
    g49: GeomPoint X=-16.9916 Y=34.7932 Z=0
    g50: GeomPoint X=-16.9916 Y=-2.78923 Z=0
  constraints (66):
    c: Coincident(g0,g1)
    c: Coincident(g1,g2)
    c: Coincident(g2,g3)
    c: Coincident(g3,g0)
    c: Horizontal(g0)
    c: Horizontal(g2)
    c: Vertical(g1)
    c: Vertical(g3)
    c: DistanceX(g2,g2) = 48.768
    c: DistanceY(g1,g1) = 29.464
    c: Coincident(g4,g0)
    c: Coincident(g4,g-10)
    c: Coincident(g5,g4)
    c: Coincident(g5,g0)
    c: Coincident(g6,g1)
    c: Coincident(g6,g-13)
    c: Equal(g6,g5)
    c: Equal(g5,g4)
    c: InternalAlignment(g8-g11 -> g7) x4
    c: Horizontal(g9)
    c: Tangent(g7,g3)
    c: Coincident(g7,g-12)
    c: DistanceY(g8,g8) = 40.386
    c: InternalAlignment(g13-g16 -> g12) x4
    c: Coincident(g12,g-11)
    c: Tangent(g12,g1)
    c: Horizontal(g14)
    c: Equal(g13,g8)
    c: InternalAlignment(g18-g21 -> g17) x4
    c: Coincident(g17,g4)
    c: Tangent(g17,g0)
    c: Vertical(g19)
    c: Block(g18)
    c: InternalAlignment(g23-g26 -> g22) x4
    c: Coincident(g22,g6)
    c: Tangent(g22,g2)
    c: Vertical(g24)
    c: Equal(g23,g18)
    c: PointOnObject(g27,g7)
    c: PointOnObject(g27,g17)
    c: PointOnObject(g28,g17)
    c: PointOnObject(g28,g12)
    c: PointOnObject(g29,g12)
    c: PointOnObject(g29,g22)
    c: PointOnObject(g30,g22)
    c: PointOnObject(g30,g7)
    c: InternalAlignment(g32-g35 -> g31) x4
    c: Coincident(g31,g4)
    c: PointOnObject(g18,g31)
    c: Coincident(g31,g28)
    c: Coincident(g31,g27)
    c: InternalAlignment(g37-g40 -> g36) x4
    c: Coincident(g36,g12)
    c: PointOnObject(g14,g36)
    c: Coincident(g36,g31)
    c: Coincident(g36,g29)
    c: InternalAlignment(g42-g45 -> g41) x4
    c: Coincident(g41,g6)
    c: PointOnObject(g23,g41)
    c: Coincident(g41,g36)
    c: Coincident(g41,g30)
    c: InternalAlignment(g47-g50 -> g46) x4
    c: Coincident(g46,g7)
    c: PointOnObject(g9,g46)
    c: Coincident(g46,g41)
    c: Coincident(g46,g31)
FEATURE [PartDesign::SubtractiveLoft] SubtractiveLoft
  BaseFeature = -> Pad003
  Closed = true
  Profile = -> Sketch012
  Ruled = false
  Sections = -> [Sketch011]
FEATURE [Sketcher::SketchObject] Sketch013
  ExternalGeometry = -> [SubtractiveLoft]
  FullyConstrained = true
  MapMode = 5
  Placement = pos=(0,38.354,-8.4e-15) rot=(0,0.707107,0.707107;3.14159rad)
  Support = -> [SubtractiveLoft]
  sketch-geometry (26):
    g0: Ellipse CenterX=0 CenterY=88.5207 CenterZ=0 NormalX=0 NormalY=0 NormalZ=1 MajorRadius=19.05 MinorRadius=1.905 AngleXU=0
    g1: LineSegment StartX=19.05 StartY=88.5207 StartZ=0 EndX=-19.05 EndY=88.5207 EndZ=0
    g2: LineSegment StartX=0 StartY=90.4257 StartZ=0 EndX=0 EndY=86.6157 EndZ=0
    g3: GeomPoint X=18.9545 Y=88.5207 Z=0
    g4: GeomPoint X=-18.9545 Y=88.5207 Z=0
    g5: Ellipse CenterX=0 CenterY=81.4077 CenterZ=0 NormalX=0 NormalY=0 NormalZ=1 MajorRadius=19.05 MinorRadius=1.905 AngleXU=0
    g6: LineSegment StartX=19.05 StartY=81.4077 StartZ=0 EndX=-19.05 EndY=81.4077 EndZ=0
    g7: LineSegment StartX=0 StartY=83.3127 StartZ=0 EndX=0 EndY=79.5027 EndZ=0
    g8: GeomPoint X=18.9545 Y=81.4077 Z=0
    g9: GeomPoint X=-18.9545 Y=81.4077 Z=0
    g10: Ellipse CenterX=0 CenterY=74.2947 CenterZ=0 NormalX=0 NormalY=0 NormalZ=1 MajorRadius=19.05 MinorRadius=1.905 AngleXU=0
    g11: LineSegment StartX=19.05 StartY=74.2947 StartZ=0 EndX=-19.05 EndY=74.2947 EndZ=0
    g12: LineSegment StartX=0 StartY=76.1997 StartZ=0 EndX=0 EndY=72.3897 EndZ=0
    g13: GeomPoint X=18.9545 Y=74.2947 Z=0
    g14: GeomPoint X=-18.9545 Y=74.2947 Z=0
    g15: Ellipse CenterX=0 CenterY=67.1816 CenterZ=0 NormalX=0 NormalY=0 NormalZ=1 MajorRadius=19.05 MinorRadius=1.905 AngleXU=0
    g16: LineSegment StartX=19.05 StartY=67.1816 StartZ=0 EndX=-19.05 EndY=67.1816 EndZ=0
    g17: LineSegment StartX=0 StartY=69.0866 StartZ=0 EndX=0 EndY=65.2766 EndZ=0
    g18: GeomPoint X=18.9545 Y=67.1816 Z=0
    g19: GeomPoint X=-18.9545 Y=67.1816 Z=0
    g20: LineSegment StartX=0 StartY=93.7288 StartZ=0 EndX=0 EndY=90.4257 EndZ=0
    g21: LineSegment StartX=0 StartY=86.6157 StartZ=0 EndX=0 EndY=83.3127 EndZ=0
    g22: LineSegment StartX=0 StartY=79.5027 StartZ=0 EndX=0 EndY=76.1997 EndZ=0
    g23: LineSegment StartX=0 StartY=72.3897 StartZ=0 EndX=0 EndY=69.0866 EndZ=0
    g24: LineSegment StartX=-22.9149 StartY=61.9736 StartZ=0 EndX=22.8603 EndY=61.9736 EndZ=0
    g25: LineSegment StartX=0 StartY=65.2766 StartZ=0 EndX=0 EndY=61.9736 EndZ=0
  constraints (38):
    c: InternalAlignment(g1-g4 -> g0) x4
    c: PointOnObject(g0,g-2)
    c: InternalAlignment(g6-g9 -> g5) x4
    c: PointOnObject(g5,g-2)
    c: InternalAlignment(g11-g14 -> g10) x4
    c: PointOnObject(g10,g-2)
    c: InternalAlignment(g16-g19 -> g15) x4
    c: PointOnObject(g15,g-2)
    c: Horizontal(g1)
    c: Horizontal(g6)
    c: Horizontal(g11)
    c: Horizontal(g16)
    c: Equal(g1,g6)
    c: Equal(g6,g11)
    c: Equal(g11,g16)
    c: Equal(g2,g7)
    c: Equal(g7,g12)
    c: Equal(g12,g17)
    c: DistanceY(g17,g17) = 3.81
    c: PointOnObject(g20,g-3)
    c: Coincident(g20,g2)
    c: Coincident(g21,g2)
    c: Coincident(g21,g7)
    c: Coincident(g22,g7)
    c: Coincident(g22,g12)
    c: Coincident(g23,g12)
    c: Coincident(g23,g17)
    c: Coincident(g24,g-6)
    c: Coincident(g24,g-5)
    c: Coincident(g25,g17)
    c: PointOnObject(g25,g24)
    c: Vertical(g25)
    c: Vertical(g20)
    c: Equal(g20,g21)
    c: Equal(g21,g22)
    c: Equal(g22,g23)
    c: Equal(g23,g25)
    c: DistanceX(g6,g6) = 38.1
FEATURE [PartDesign::Pocket] Pocket005
  BaseFeature = -> SubtractiveLoft
  Direction = (0,-1,2e-16)
  Length = 25.4
  Length2 = 5.08
  Profile = -> Sketch013
  ReferenceAxis = -> Sketch013 [N_Axis]
  Type = 0
FEATURE [Sketcher::SketchObject] Sketch014
  FullyConstrained = true
  MapMode = 5
  Placement = pos=(0,1.36e-14,61.9736) rot=(1,0,0;3.14159rad)
  Support = -> [Pocket005]
  sketch-geometry (8):
    g0: ArcOfEllipse CenterX=-16.9913 CenterY=-16.009 CenterZ=0 NormalX=0 NormalY=0 NormalZ=1 MajorRadius=25.228 MinorRadius=10.2379 AngleXU=1.57081 StartAngle=0.883334 EndAngle=2.26788
    g1: ArcOfEllipse CenterX=17.0444 CenterY=-16.002 CenterZ=0 NormalX=0 NormalY=0 NormalZ=1 MajorRadius=25.2216 MinorRadius=10.2377 AngleXU=1.5708 StartAngle=4.01562 EndAngle=5.39969
    g2: ArcOfEllipse CenterX=0 CenterY=-27.305 CenterZ=0 NormalX=0 NormalY=0 NormalZ=1 MajorRadius=31.7344 MinorRadius=7.874 AngleXU=2.21e-14 StartAngle=3.81329 EndAngle=5.61429
    g3: LineSegment StartX=24.9577 StartY=0 StartZ=0 EndX=43.3153 EndY=0 EndZ=0
    g4: LineSegment StartX=43.3153 StartY=0 StartZ=0 EndX=39.9601 EndY=-85.6362 EndZ=0
    g5: LineSegment StartX=39.9601 StartY=-85.6362 StartZ=0 EndX=-41.1692 EndY=-81.4353 EndZ=0
    g6: LineSegment StartX=-41.1692 StartY=-81.4353 StartZ=0 EndX=-48.0718 EndY=0 EndZ=0
    g7: LineSegment StartX=-48.0718 StartY=0 StartZ=0 EndX=-24.904 EndY=0 EndZ=0
  constraints (19):
    c: PointOnObject(g2,g-2)
    c: Coincident(g2,g1)
    c: Coincident(g2,g0)
    c: Block(g2)
    c: Coincident(g3,g1)
    c: Horizontal(g3)
    c: Coincident(g4,g3)
    c: Coincident(g5,g4)
    c: Coincident(g6,g5)
    c: PointOnObject(g6,g-1)
    c: PointOnObject(g0,g-1)
    c: Block(g0)
    c: PointOnObject(g1,g-1)
    c: Block(g1)
    c: Coincident(g7,g6)
    c: Coincident(g7,g0)
    c: Block(g5)
    c: Block(g3)
    c: Block(g7)
FEATURE [Sketcher::SketchObject] Sketch015
  ExternalGeometry = -> [Sketch014]
  FullyConstrained = false
  MapMode = 5
  Placement = pos=(0,2.06e-14,93.7288) rot=(0,0,1;0rad)
  Support = -> [Pocket005]
  sketch-geometry (24):
    g0: GeomPoint X=0 Y=35.179 Z=0
    g1: GeomPoint X=0 Y=32.004 Z=0
    g2: LineSegment StartX=-24.8479 StartY=32.2038 StartZ=0 EndX=-23.8541 EndY=31.5541 EndZ=0
    g3: LineSegment StartX=-23.8541 StartY=31.5541 StartZ=0 EndX=-22.8603 EndY=30.9043 EndZ=0
    g4: LineSegment StartX=0 StartY=35.179 StartZ=0 EndX=0 EndY=33.5915 EndZ=0
    g5: LineSegment StartX=0 StartY=33.5915 StartZ=0 EndX=0 EndY=32.004 EndZ=0
    g6: LineSegment StartX=22.9149 StartY=30.8983 StartZ=0 EndX=23.9054 EndY=31.5431 EndZ=0
    g7: LineSegment StartX=23.9054 StartY=31.5431 StartZ=0 EndX=24.8959 EndY=32.1878 EndZ=0
    g8: LineSegment StartX=24.9184 StartY=16.002 StartZ=0 EndX=26.1002 EndY=16.002 EndZ=0
    g9: LineSegment StartX=26.1002 StartY=16.002 StartZ=0 EndX=27.2821 EndY=16.002 EndZ=0
    g10: LineSegment StartX=-24.8656 StartY=16.002 StartZ=0 EndX=-26.0474 EndY=16.002 EndZ=0
    g11: LineSegment StartX=-26.0474 StartY=16.002 StartZ=0 EndX=-27.2292 EndY=16.002 EndZ=0
    g12: ArcOfEllipse CenterX=-1.06966e-10 CenterY=19.2659 CenterZ=0 NormalX=0 NormalY=0 NormalZ=1 MajorRadius=46.3988 MinorRadius=14.3256 AngleXU=-3.47212e-05 StartAngle=1.02955 EndAngle=2.11078
    g13: ArcOfEllipse CenterX=-17.0128 CenterY=16.002 CenterZ=0 NormalX=0 NormalY=0 NormalZ=1 MajorRadius=23.8109 MinorRadius=9.03459 AngleXU=1.5708 StartAngle=0.859061 EndAngle=2.2393
    g14: GeomPoint X=-17.0128 Y=38.0323 Z=0
    g15: ArcOfEllipse CenterX=17.0444 CenterY=16.002 CenterZ=0 NormalX=0 NormalY=0 NormalZ=1 MajorRadius=23.8111 MinorRadius=9.05586 AngleXU=1.5708 StartAngle=3.97543 EndAngle=5.42351
    g16: GeomPoint X=17.0444 Y=38.0238 Z=0
    g17: LineSegment StartX=-48.0718 StartY=0 StartZ=0 EndX=-23.703 EndY=0 EndZ=0
    g18: LineSegment StartX=43.3153 StartY=3.6e-15 StartZ=0 EndX=23.7504 EndY=3.6e-15 EndZ=0
    g19: ArcOfEllipse CenterX=-17.0128 CenterY=16.002 CenterZ=0 NormalX=0 NormalY=0 NormalZ=1 MajorRadius=23.8109 MinorRadius=9.03459 AngleXU=1.5708 StartAngle=0.859061 EndAngle=2.30777
    g20: GeomPoint X=-17.0128 Y=38.0323 Z=0
    g21: LineSegment StartX=-48.0718 StartY=0 StartZ=0 EndX=-41.1692 EndY=81.4353 EndZ=0
    g22: LineSegment StartX=-41.1692 StartY=81.4353 StartZ=0 EndX=39.9601 EndY=85.6362 EndZ=0
    g23: LineSegment StartX=39.9601 StartY=85.6362 StartZ=0 EndX=43.3153 EndY=0 EndZ=0
  constraints (46):
    c: PointOnObject(g0,g-2)
    c: PointOnObject(g1,g-2)
    c: Coincident(g3,g2)
    c: Parallel(g2,g3)
    c: Equal(g2,g3)
    c: Coincident(g4,g0)
    c: PointOnObject(g4,g-2)
    c: Coincident(g5,g4)
    c: Coincident(g5,g1)
    c: Equal(g5,g4)
    c: Coincident(g7,g6)
    c: Parallel(g6,g7)
    c: Equal(g6,g7)
    c: Horizontal(g8)
    c: Coincident(g9,g8)
    c: Horizontal(g9)
    c: Horizontal(g10)
    c: Coincident(g11,g10)
    c: Horizontal(g11)
    c: Equal(g11,g10)
    c: Equal(g8,g9)
    c: Coincident(g12,g2)
    c: PointOnObject(g12,g7)
    c: Block(g12)
    c: InternalAlignment(g14,g13)
    c: PointOnObject(g10,g13)
    c: PointOnObject(g12,g13)
    c: InternalAlignment(g16,g15)
    c: PointOnObject(g8,g15)
    c: Coincident(g17,g-3)
    c: Coincident(g18,g-4)
    c: Horizontal(g18)
    c: Horizontal(g17)
    c: PointOnObject(g13,g2)
    c: PointOnObject(g17,g13)
    c: Coincident(g15,g18)
    c: Coincident(g15,g12)
    c: InternalAlignment(g20,g19)
    c: PointOnObject(g10,g19)
    c: Coincident(g19,g13)
    c: PointOnObject(g19,g17)
    c: Coincident(g21,g17)
    c: Coincident(g22,g21)
    c: Coincident(g22,g-5)
    c: Coincident(g23,g18)
    c: Coincident(g23,g22)
FEATURE [PartDesign::SubtractiveLoft] SubtractiveLoft001
  BaseFeature = -> Pocket005
  Closed = true
  Profile = -> Sketch015
  Ruled = false
  Sections = -> [Sketch014]
FEATURE [Sketcher::SketchObject] Sketch016
  ExternalGeometry = -> [SubtractiveLoft001]
  FullyConstrained = true
  MapMode = 5
  Placement = pos=(0,-3.175,0) rot=(1,0,0;1.5708rad)
  Support = -> [SubtractiveLoft001]
  sketch-geometry (8):
    g0: LineSegment StartX=-9.52073 StartY=76.6533 StartZ=0 EndX=9.52927 EndY=76.6533 EndZ=0
    g1: LineSegment StartX=9.52927 StartY=76.6533 StartZ=0 EndX=9.52927 EndY=63.9533 EndZ=0
    g2: LineSegment StartX=9.52927 StartY=63.9533 StartZ=0 EndX=-9.52073 EndY=63.9533 EndZ=0
    g3: LineSegment StartX=-9.52073 StartY=63.9533 StartZ=0 EndX=-9.52073 EndY=76.6533 EndZ=0
    g4: LineSegment StartX=-15.077 StartY=25.4 StartZ=0 EndX=-9.52073 EndY=63.9533 EndZ=0
    g5: LineSegment StartX=15.0855 StartY=25.4 StartZ=0 EndX=9.52927 EndY=63.9533 EndZ=0
    g6: LineSegment StartX=-15.077 StartY=0.453278 StartZ=0 EndX=15.0855 EndY=0.453278 EndZ=0
    g7: LineSegment StartX=-9.52073 StartY=63.9533 StartZ=0 EndX=-9.52073 EndY=0.453278 EndZ=0
  constraints (21):
    c: Coincident(g0,g1)
    c: Coincident(g1,g2)
    c: Coincident(g2,g3)
    c: Coincident(g3,g0)
    c: Horizontal(g0)
    c: Horizontal(g2)
    c: Vertical(g1)
    c: Vertical(g3)
    c: DistanceY(g1,g1) = 12.7
    c: DistanceX(g2,g2) = 19.05
    c: Coincident(g4,g2)
    c: Coincident(g5,g-3)
    c: Coincident(g5,g1)
    c: Equal(g5,g4)
    c: Coincident(g4,g-4)
    c: Coincident(g6,g-4)
    c: Coincident(g6,g-3)
    c: Coincident(g7,g2)
    c: PointOnObject(g7,g6)
    c: Vertical(g7)
    c: DistanceY(g7,g7) = 63.5
FEATURE [PartDesign::Pocket] Pocket006
  BaseFeature = -> SubtractiveLoft001
  Direction = (0,1,-2e-16)
  Length = 30.48
  Length2 = 81.28
  Profile = -> Sketch016
  ReferenceAxis = -> Sketch016 [N_Axis]
  Type = 4
FEATURE [Sketcher::SketchObject] Sketch017
  ExternalGeometry = -> [Pocket006]
  FullyConstrained = true
  MapMode = 5
  Placement = pos=(0,-3.175,7e-16) rot=(1,0,0;1.5708rad)
  Support = -> [Pocket006]
  sketch-geometry (4):
    g0: LineSegment StartX=-9.52073 StartY=63.9533 StartZ=0 EndX=9.52927 EndY=63.9533 EndZ=0
    g1: LineSegment StartX=9.52927 StartY=63.9533 StartZ=0 EndX=9.52927 EndY=76.6533 EndZ=0
    g2: LineSegment StartX=9.52927 StartY=76.6533 StartZ=0 EndX=-9.52073 EndY=76.6533 EndZ=0
    g3: LineSegment StartX=-9.52073 StartY=76.6533 StartZ=0 EndX=-9.52073 EndY=63.9533 EndZ=0
  constraints (10):
    c: Coincident(g0,g1)
    c: Coincident(g1,g2)
    c: Coincident(g2,g3)
    c: Coincident(g3,g0)
    c: Horizontal(g0)
    c: Horizontal(g2)
    c: Vertical(g1)
    c: Vertical(g3)
    c: Coincident(g0,g-4)
    c: Coincident(g1,g-5)
FEATURE [PartDesign::Pocket] Pocket007
  BaseFeature = -> Pocket006
  Direction = (0,1,-2e-16)
  Length = 5.08
  Length2 = 5.08
  Profile = -> Sketch017
  ReferenceAxis = -> Sketch017 [N_Axis]
  Type = 0
FEATURE [Sketcher::SketchObject] Sketch018
  FullyConstrained = false
  MapMode = 5
  Placement = pos=(0,0,0) rot=(1,0,0;1.5708rad)
  Support = -> [XZ_Plane]
  sketch-geometry (20):
    g0: LineSegment StartX=-111.248 StartY=38.5596 StartZ=0 EndX=-3.4846 EndY=146.323 EndZ=0
    g1: LineSegment StartX=5.49566 StartY=-78.1837 StartZ=0 EndX=113.259 EndY=29.5793 EndZ=0
    g2: LineSegment StartX=-111.248 StartY=38.5596 StartZ=0 EndX=5.49566 EndY=-78.1837 EndZ=0
    g3: LineSegment StartX=-3.4846 StartY=146.323 StartZ=0 EndX=113.259 EndY=29.5793 EndZ=0
    g4: LineSegment StartX=-89.1791 StartY=16.491 StartZ=0 EndX=-95.7951 EndY=54.0122 EndZ=0
    g5: LineSegment StartX=20.9482 StartY=-62.7311 StartZ=0 EndX=-16.5729 EndY=-56.1151 EndZ=0
    g6: LineSegment StartX=86.7273 StartY=3.04787 StartZ=0 EndX=108.581 EndY=34.2576 EndZ=0
    g7: LineSegment StartX=1.19362 StartY=141.644 StartZ=0 EndX=-30.0161 EndY=119.791 EndZ=0
    g8: ArcOfCircle CenterX=-95.0597 CenterY=-61.9958 CenterZ=0 NormalX=0 NormalY=0 NormalZ=1 AngleXU=0 Radius=78.7068 StartAngle=0.0747857 EndAngle=1.49601
    g9: LineSegment StartX=-52.876 StartY=-19.8121 StartZ=0 EndX=-39.4056 EndY=-6.34168 EndZ=0
    g10: ArcOfCircle CenterX=210.915 CenterY=243.979 CenterZ=0 NormalX=0 NormalY=0 NormalZ=1 AngleXU=0 Radius=233.357 StartAngle=3.59556 EndAngle=4.25842
    g11: LineSegment StartX=54.8871 StartY=87.951 StartZ=0 EndX=45.9068 EndY=78.9708 EndZ=0
    g12: ArcOfCircle CenterX=-96.3222 CenterY=120.318 CenterZ=0 NormalX=0 NormalY=0 NormalZ=1 AngleXU=0 Radius=66.3082 StartAngle=4.72034 EndAngle=6.27524
    g13: ArcOfCircle CenterX=87.2543 CenterY=-63.2582 CenterZ=0 NormalX=0 NormalY=0 NormalZ=1 AngleXU=0 Radius=66.3082 StartAngle=1.57875 EndAngle=3.13364
    g14: LineSegment StartX=-62.9056 StartY=86.9017 StartZ=0 EndX=-49.4352 EndY=73.4313 EndZ=0
    g15: LineSegment StartX=40.3674 StartY=-16.3712 StartZ=0 EndX=53.8378 EndY=-29.8416 EndZ=0
    g16: LineSegment StartX=-17.7449 StartY=81.8177 StartZ=0 EndX=17.0135 EndY=81.8177 EndZ=0
    g17: LineSegment StartX=17.0135 StartY=81.8177 StartZ=0 EndX=17.0135 EndY=-13.5537 EndZ=0
    g18: LineSegment StartX=17.0135 StartY=-13.5537 StartZ=0 EndX=-17.7449 EndY=-13.5537 EndZ=0
    g19: LineSegment StartX=-17.7449 StartY=-13.5537 StartZ=0 EndX=-17.7449 EndY=81.8177 EndZ=0
  constraints (69):
    c: Angle(g0) = 0.785398
    c: Parallel(g1,g0)
    c: Coincident(g2,g0)
    c: Coincident(g2,g1)
    c: Coincident(g3,g1)
    c: Perpendicular(g3,g1)
    c: Distance(g2) = 165.1
    c: Distance(g1) = 152.4
    c: Equal(g1,g0)
    c: PointOnObject(g4,g2)
    c: PointOnObject(g4,g0)
    c: Angle(g2,g4) = 2.53073
    c: Distance(g4) = 38.1
    c: PointOnObject(g5,g1)
    c: PointOnObject(g5,g2)
    c: Angle(g5,g2) = 2.53073
    c: Distance(g5) = 38.1
    c: PointOnObject(g6,g1)
    c: PointOnObject(g6,g3)
    c: PointOnObject(g7,g3)
    c: PointOnObject(g7,g0)
    c: Equal(g7,g6)
    c: Equal(g6,g5)
    c: Angle(g6,g1) = 2.96706
    c: Angle(g0,g7) = 2.96706
    c: PointOnObject(g4,g8)
    c: PointOnObject(g5,g8)
    c: PointOnObject(g9,g2)
    c: PointOnObject(g9,g8)
    c: Perpendicular(g2,g9)
    c: Perpendicular(g8,g9)
    c: Distance(g9) = 19.05
    c: PointOnObject(g8,g2)
    c: PointOnObject(g8,g2)
    c: PointOnObject(g7,g10)
    c: PointOnObject(g11,g3)
    c: PointOnObject(g11,g10)
    c: Perpendicular(g3,g11)
    c: Perpendicular(g10,g11)
    c: Distance(g11) = 12.7
    c: PointOnObject(g6,g10)
    c: PointOnObject(g10,g3)
    c: PointOnObject(g10,g3)
    c: PointOnObject(g4,g12)
    c: PointOnObject(g7,g12)
    c: PointOnObject(g14,g0)
    c: PointOnObject(g14,g12)
    c: PointOnObject(g15,g13)
    c: PointOnObject(g15,g1)
    c: Perpendicular(g1,g15)
    c: Perpendicular(g13,g15)
    c: Perpendicular(g12,g14)
    c: Perpendicular(g0,g14)
    c: Distance(g14) = 19.05
    c: Equal(g14,g15)
    c: PointOnObject(g12,g0)
    c: PointOnObject(g12,g0)
    c: Coincident(g13,g5)
    c: Coincident(g13,g6)
    c: Coincident(g16,g17)
    c: Coincident(g17,g18)
    c: Coincident(g18,g19)
    c: Coincident(g19,g16)
    c: Horizontal(g16)
    c: Horizontal(g18)
    c: Vertical(g17)
    c: Vertical(g19)
    c: Coincident(g0,g3)
    c: Block(g10)
FEATURE [PartDesign::Pad] Pad004
  AlongSketchNormal = false
  BaseFeature = -> Pocket007
  Direction = (0,-1,-2e-16)
  Length = 3.302
  Length2 = 9.906
  Profile = -> Sketch018
  ReferenceAxis = -> Sketch018 [N_Axis]
  Type = 0
FEATURE [Sketcher::SketchObject] Sketch019
  ExternalGeometry = -> [Pad004]
  FullyConstrained = false
  MapMode = 5
  Placement = pos=(0,-1e-16,0) rot=(0,0.707107,0.707107;3.14159rad)
  Support = -> [Pad004]
  sketch-geometry (17):
    g0: LineSegment StartX=10.6155 StartY=133.376 StartZ=0 EndX=24.9437 EndY=123.343 EndZ=0
    g1: LineSegment StartX=93.4336 StartY=40.6193 StartZ=0 EndX=90.7947 EndY=25.6538 EndZ=0
    g2: LineSegment StartX=-100.312 StartY=22.4485 StartZ=0 EndX=-90.279 EndY=8.12025 EndZ=0
    g3: LineSegment StartX=-7.55535 StartY=-60.3696 StartZ=0 EndX=7.41018 EndY=-57.7308 EndZ=0
    g4: ArcOfCircle CenterX=-87.2543 CenterY=-63.2582 CenterZ=0 NormalX=0 NormalY=0 NormalZ=1 AngleXU=0 Radius=66.3082 StartAngle=0.196116 EndAngle=1.47727
    g5: ArcOfCircle CenterX=95.0597 CenterY=-61.9958 CenterZ=0 NormalX=0 NormalY=0 NormalZ=1 AngleXU=0 Radius=78.7068 StartAngle=1.75533 EndAngle=2.95706
    g6: ArcOfCircle CenterX=96.3222 CenterY=120.318 CenterZ=0 NormalX=0 NormalY=0 NormalZ=1 AngleXU=0 Radius=66.3082 StartAngle=3.23512 EndAngle=4.51627
    g7: ArcOfCircle CenterX=-210.915 CenterY=243.979 CenterZ=0 NormalX=0 NormalY=0 NormalZ=1 AngleXU=0 Radius=233.357 StartAngle=5.22653 EndAngle=5.76905
    g8: ArcOfCircle CenterX=-89.9085 CenterY=29.7329 CenterZ=0 NormalX=0 NormalY=0 NormalZ=1 AngleXU=0 Radius=12.7 StartAngle=2.08493 EndAngle=3.75246
    g9: ArcOfCircle CenterX=3.33106 CenterY=122.972 CenterZ=0 NormalX=0 NormalY=0 NormalZ=1 AngleXU=0 Radius=12.7 StartAngle=0.959931 EndAngle=2.62746
    g10: ArcOfCircle CenterX=17.6593 CenterY=112.94 CenterZ=0 NormalX=0 NormalY=0 NormalZ=1 AngleXU=0 Radius=12.7 StartAngle=0.0935264 EndAngle=0.959931
    g11: ArcOfCircle CenterX=80.9265 CenterY=42.8246 CenterZ=0 NormalX=0 NormalY=0 NormalZ=1 AngleXU=0 Radius=12.7 StartAngle=6.10865 EndAngle=7.65787
    g12: ArcOfCircle CenterX=78.2877 CenterY=27.8591 CenterZ=0 NormalX=0 NormalY=0 NormalZ=1 AngleXU=0 Radius=12.7 StartAngle=4.89692 EndAngle=6.10865
    g13: ArcOfCircle CenterX=5.20484 CenterY=-45.2237 CenterZ=0 NormalX=0 NormalY=0 NormalZ=1 AngleXU=0 Radius=12.7 StartAngle=4.88692 EndAngle=6.09865
    g14: ArcOfCircle CenterX=-9.76068 CenterY=-47.8625 CenterZ=0 NormalX=0 NormalY=0 NormalZ=1 AngleXU=0 Radius=12.7 StartAngle=3.33771 EndAngle=4.88692
    g15: ArcOfCircle CenterX=-79.8757 CenterY=15.4047 CenterZ=0 NormalX=0 NormalY=0 NormalZ=1 AngleXU=0 Radius=12.7 StartAngle=3.75246 EndAngle=4.61886
    g16: Circle CenterX=-31.6291 CenterY=34.7013 CenterZ=0 NormalX=0 NormalY=0 NormalZ=1 AngleXU=0 Radius=404.916
  constraints (40):
    c: Coincident(g4,g-8)
    c: Coincident(g5,g-6)
    c: Coincident(g6,g-4)
    c: Coincident(g7,g-10)
    c: Tangent(g7,g8) = 1.5708
    c: Tangent(g2,g8) = -1.5708
    c: Tangent(g7,g9) = 1.5708
    c: Tangent(g0,g9) = 1.5708
    c: Tangent(g0,g10) = 1.5708
    c: Tangent(g6,g10) = 1.5708
    c: Tangent(g6,g11) = 1.5708
    c: Tangent(g1,g11) = 1.5708
    c: Tangent(g5,g12) = 1.5708
    c: Tangent(g1,g12) = 1.5708
    c: Tangent(g5,g13) = 1.5708
    c: Tangent(g3,g13) = -1.5708
    c: Tangent(g3,g14) = -1.5708
    c: Tangent(g4,g14) = 1.5708
    c: Tangent(g2,g15) = -1.5708
    c: Tangent(g4,g15) = 1.5708
    c: Equal(g8,g15)
    c: Equal(g15,g14)
    c: Equal(g14,g13)
    c: Equal(g13,g12)
    c: Equal(g12,g11)
    c: Equal(g11,g9)
    c: Equal(g9,g10)
    c: PointOnObject(g7,g-10)
    c: PointOnObject(g2,g-9)
    c: PointOnObject(g2,g-9)
    c: PointOnObject(g3,g-7)
    c: PointOnObject(g3,g-7)
    c: PointOnObject(g4,g-8)
    c: PointOnObject(g5,g-6)
    c: PointOnObject(g1,g-5)
    c: PointOnObject(g1,g-5)
    c: PointOnObject(g6,g-4)
    c: PointOnObject(g0,g-3)
    c: PointOnObject(g0,g-3)
    c: Radius(g8) = 12.7
FEATURE [PartDesign::Pocket] Pocket008
  BaseFeature = -> Pad004
  Direction = (0,-1,-2e-16)
  Length = 5.08
  Length2 = 5.08
  Profile = -> Sketch019
  ReferenceAxis = -> Sketch019 [N_Axis]
  Type = 1
FEATURE [Sketcher::SketchObject] Sketch020
  ExternalGeometry = -> [Pocket008]
  FullyConstrained = true
  MapMode = 5
  Placement = pos=(0,-1e-16,0) rot=(0,0.707107,0.707107;3.14159rad)
  Support = -> [Pocket008]
  sketch-geometry (48):
    g0: ArcOfCircle CenterX=-89.8994 CenterY=32.4381 CenterZ=0 NormalX=0 NormalY=0 NormalZ=1 AngleXU=0 Radius=3.175 StartAngle=0.610865 EndAngle=3.75246
    g1: ArcOfCircle CenterX=-75.3306 CenterY=11.6317 CenterZ=0 NormalX=0 NormalY=0 NormalZ=1 AngleXU=0 Radius=3.175 StartAngle=3.75246 EndAngle=6.89405
    g2: LineSegment StartX=-92.5002 StartY=30.617 StartZ=0 EndX=-77.9314 EndY=9.81057 EndZ=0
    g3: LineSegment StartX=-72.7298 StartY=13.4528 StartZ=0 EndX=-87.2986 EndY=34.2592 EndZ=0
    g4: ArcOfCircle CenterX=-79.4962 CenterY=39.7226 CenterZ=0 NormalX=0 NormalY=0 NormalZ=1 AngleXU=0 Radius=3.175 StartAngle=0.610865 EndAngle=3.75246
    g5: ArcOfCircle CenterX=-64.9273 CenterY=18.9161 CenterZ=0 NormalX=0 NormalY=0 NormalZ=1 AngleXU=0 Radius=3.175 StartAngle=3.75246 EndAngle=6.89405
    g6: LineSegment StartX=-82.097 StartY=37.9015 StartZ=0 EndX=-67.5282 EndY=17.095 EndZ=0
    g7: LineSegment StartX=-62.3265 StartY=20.7372 StartZ=0 EndX=-76.8954 EndY=41.5437 EndZ=0
    g8: ArcOfCircle CenterX=0.625811 CenterY=122.963 CenterZ=0 NormalX=0 NormalY=0 NormalZ=1 AngleXU=0 Radius=3.175 StartAngle=0.959931 EndAngle=4.10152
    g9: ArcOfCircle CenterX=21.4323 CenterY=108.395 CenterZ=0 NormalX=0 NormalY=0 NormalZ=1 AngleXU=0 Radius=3.175 StartAngle=4.10152 EndAngle=7.24312
    g10: LineSegment StartX=-1.19529 StartY=120.363 StartZ=0 EndX=19.6112 EndY=105.794 EndZ=0
    g11: LineSegment StartX=23.2534 StartY=110.995 StartZ=0 EndX=2.44692 EndY=125.564 EndZ=0
    g12: ArcOfCircle CenterX=-6.65861 CenterY=112.56 CenterZ=0 NormalX=0 NormalY=0 NormalZ=1 AngleXU=0 Radius=3.175 StartAngle=0.959931 EndAngle=4.10152
    g13: ArcOfCircle CenterX=14.1479 CenterY=97.9913 CenterZ=0 NormalX=0 NormalY=0 NormalZ=1 AngleXU=0 Radius=3.175 StartAngle=4.10152 EndAngle=7.24312
    g14: LineSegment StartX=-8.47972 StartY=109.959 StartZ=0 EndX=12.3267 EndY=95.3905 EndZ=0
    g15: LineSegment StartX=15.969 StartY=100.592 StartZ=0 EndX=-4.83751 EndY=115.161 EndZ=0
    g16: ArcOfCircle CenterX=80.277 CenterY=48.1197 CenterZ=0 NormalX=0 NormalY=0 NormalZ=1 AngleXU=0 Radius=3.175 StartAngle=6.10865 EndAngle=9.25025
    g17: ArcOfCircle CenterX=75.8664 CenterY=23.1055 CenterZ=0 NormalX=0 NormalY=0 NormalZ=1 AngleXU=0 Radius=3.175 StartAngle=2.96706 EndAngle=6.10865
    g18: LineSegment StartX=77.1503 StartY=48.671 StartZ=0 EndX=72.7396 EndY=23.6569 EndZ=0
    g19: LineSegment StartX=78.9931 StartY=22.5542 StartZ=0 EndX=83.4038 EndY=47.5683 EndZ=0
    g20: ArcOfCircle CenterX=67.77 CenterY=50.325 CenterZ=0 NormalX=0 NormalY=0 NormalZ=1 AngleXU=0 Radius=3.175 StartAngle=6.10865 EndAngle=9.25025
    g21: ArcOfCircle CenterX=63.3593 CenterY=25.3109 CenterZ=0 NormalX=0 NormalY=0 NormalZ=1 AngleXU=0 Radius=3.175 StartAngle=2.96706 EndAngle=6.10865
    g22: LineSegment StartX=64.6432 StartY=50.8763 StartZ=0 EndX=60.2325 EndY=25.8622 EndZ=0
    g23: LineSegment StartX=66.4861 StartY=24.7595 StartZ=0 EndX=70.8967 EndY=49.7737 EndZ=0
    g24: ArcOfCircle CenterX=9.95841 CenterY=-42.8024 CenterZ=0 NormalX=0 NormalY=0 NormalZ=1 AngleXU=0 Radius=3.175 StartAngle=4.88692 EndAngle=8.02851
    g25: ArcOfCircle CenterX=-15.0557 CenterY=-47.2131 CenterZ=0 NormalX=0 NormalY=0 NormalZ=1 AngleXU=0 Radius=3.175 StartAngle=1.74533 EndAngle=4.88692
    g26: LineSegment StartX=9.40708 StartY=-39.6756 StartZ=0 EndX=-15.607 EndY=-44.0863 EndZ=0
    g27: LineSegment StartX=-14.5044 StartY=-50.3398 StartZ=0 EndX=10.5097 EndY=-45.9292 EndZ=0
    g28: ArcOfCircle CenterX=7.75308 CenterY=-30.2953 CenterZ=0 NormalX=0 NormalY=0 NormalZ=1 AngleXU=0 Radius=3.175 StartAngle=4.88692 EndAngle=8.02851
    g29: ArcOfCircle CenterX=-17.261 CenterY=-34.706 CenterZ=0 NormalX=0 NormalY=0 NormalZ=1 AngleXU=0 Radius=3.175 StartAngle=1.74533 EndAngle=4.88692
    g30: LineSegment StartX=7.20174 StartY=-27.1686 StartZ=0 EndX=-17.8124 EndY=-31.5792 EndZ=0
    g31: LineSegment StartX=-16.7097 StartY=-37.8328 StartZ=0 EndX=8.30441 EndY=-33.4221 EndZ=0
    g32: LineSegment StartX=-15.607 StartY=-44.0863 StartZ=0 EndX=-16.7097 EndY=-37.8328 EndZ=0
    g33: LineSegment StartX=-87.2986 StartY=34.2592 StartZ=0 EndX=-82.097 EndY=37.9015 EndZ=0
    g34: LineSegment StartX=15.969 StartY=100.592 StartZ=0 EndX=19.6112 EndY=105.794 EndZ=0
    g35: LineSegment StartX=66.4861 StartY=24.7595 StartZ=0 EndX=72.7396 EndY=23.6569 EndZ=0
    g36: LineSegment StartX=10.6155 StartY=133.376 StartZ=0 EndX=4.25792 EndY=124.296 EndZ=0
    g37: LineSegment StartX=93.4336 StartY=40.6193 StartZ=0 EndX=82.5179 EndY=42.544 EndZ=0
    g38: LineSegment StartX=7.41018 StartY=-57.7308 StartZ=0 EndX=5.48545 EndY=-46.8151 EndZ=0
    g39: LineSegment StartX=-100.312 StartY=22.4485 StartZ=0 EndX=-91.2321 EndY=28.806 EndZ=0
    g40: LineSegment StartX=-76.8283 StartY=2.22516 StartZ=0 EndX=-75.8298 EndY=8.49617 EndZ=0
    g41: LineSegment StartX=-81.2141 StartY=42.3926 StartZ=0 EndX=-84.65 EndY=47.7328 EndZ=0
    g42: LineSegment StartX=-9.32869 StartY=114.278 StartZ=0 EndX=-14.6689 EndY=117.714 EndZ=0
    g43: LineSegment StartX=24.5678 StartY=108.894 StartZ=0 EndX=30.8388 EndY=109.892 EndZ=0
    g44: LineSegment StartX=79.8905 StartY=51.271 StartZ=0 EndX=79.3803 EndY=55.4302 EndZ=0
    g45: LineSegment StartX=74.4253 StartY=20.2764 StartZ=0 EndX=72.5234 EndY=16.5426 EndZ=0
    g46: LineSegment StartX=12.7875 StartY=-41.3613 StartZ=0 EndX=16.5213 EndY=-39.4595 EndZ=0
    g47: LineSegment StartX=-22.3662 StartY=-46.3164 StartZ=0 EndX=-18.2071 EndY=-46.8265 EndZ=0
  constraints (132):
    c: Tangent(g0,g2) = -1.5708
    c: Tangent(g2,g1) = -1.5708
    c: Tangent(g1,g3) = -1.5708
    c: Tangent(g3,g0) = -1.5708
    c: Equal(g0,g1)
    c: Tangent(g4,g6) = -1.5708
    c: Tangent(g6,g5) = -1.5708
    c: Tangent(g5,g7) = -1.5708
    c: Tangent(g7,g4) = -1.5708
    c: Equal(g4,g5)
    c: Tangent(g8,g10) = -1.5708
    c: Tangent(g10,g9) = -1.5708
    c: Tangent(g9,g11) = -1.5708
    c: Tangent(g11,g8) = -1.5708
    c: Equal(g8,g9)
    c: Tangent(g12,g14) = -1.5708
    c: Tangent(g14,g13) = -1.5708
    c: Tangent(g13,g15) = -1.5708
    c: Tangent(g15,g12) = -1.5708
    c: Equal(g12,g13)
    c: Tangent(g16,g18) = -1.5708
    c: Tangent(g18,g17) = -1.5708
    c: Tangent(g17,g19) = -1.5708
    c: Tangent(g19,g16) = -1.5708
    c: Equal(g16,g17)
    c: Tangent(g20,g22) = -1.5708
    c: Tangent(g22,g21) = -1.5708
    c: Tangent(g21,g23) = -1.5708
    c: Tangent(g23,g20) = -1.5708
    c: Equal(g20,g21)
    c: Tangent(g24,g26) = -1.5708
    c: Tangent(g26,g25) = -1.5708
    c: Tangent(g25,g27) = -1.5708
    c: Tangent(g27,g24) = -1.5708
    c: Equal(g24,g25)
    c: Tangent(g28,g30) = -1.5708
    c: Tangent(g30,g29) = -1.5708
    c: Tangent(g29,g31) = -1.5708
    c: Tangent(g31,g28) = -1.5708
    c: Equal(g28,g29)
    c: Equal(g3,g6)
    c: Equal(g6,g14)
    c: Equal(g14,g10)
    c: Equal(g10,g22)
    c: Equal(g22,g18)
    c: Equal(g18,g30)
    c: Equal(g30,g26)
    c: Distance(g30) = 25.4
    c: Equal(g0,g4)
    c: Equal(g4,g12)
    c: Equal(g12,g8)
    c: Equal(g8,g20)
    c: Equal(g20,g16)
    c: Equal(g16,g29)
    c: Equal(g29,g25)
    c: Radius(g28) = 3.175
    c: Parallel(g-17,g2)
    c: Parallel(g2,g6)
    c: Parallel(g-5,g11)
    c: Parallel(g11,g15)
    c: Parallel(g-9,g19)
    c: Parallel(g19,g23)
    c: Parallel(g-13,g26)
    c: Parallel(g26,g31)
    c: Coincident(g32,g25)
    c: Coincident(g32,g29)
    c: Perpendicular(g-13,g32)
    c: Coincident(g33,g0)
    c: Coincident(g33,g4)
    c: Perpendicular(g-17,g33)
    c: Coincident(g34,g13)
    c: Coincident(g34,g9)
    c: Perpendicular(g-5,g34)
    c: Coincident(g35,g21)
    c: Perpendicular(g-9,g35)
    c: Coincident(g35,g17)
    c: Equal(g32,g33)
    c: Equal(g33,g35)
    c: Equal(g35,g34)
    c: Distance(g34) = 6.35
    c: Coincident(g36,g-5)
    c: PointOnObject(g36,g11)
    c: Perpendicular(g11,g36)
    c: Coincident(g37,g-9)
    c: PointOnObject(g37,g19)
    c: Perpendicular(g-9,g37)
    c: Equal(g37,g36)
    c: Coincident(g38,g-13)
    c: PointOnObject(g38,g27)
    c: Perpendicular(g-13,g38)
    c: Equal(g38,g37)
    c: Coincident(g39,g-18)
    c: PointOnObject(g39,g2)
    c: Perpendicular(g-17,g39)
    c: Equal(g39,g38)
    c: PointOnObject(g40,g-15)
    c: PointOnObject(g40,g1)
    c: PointOnObject(g41,g4)
    c: Equal(g41,g40)
    c: PointOnObject(g41,g-3)
    c: Perpendicular(g-3,g41)
    c: Perpendicular(g-15,g40)
    c: Perpendicular(g1,g40)
    c: Perpendicular(g4,g41)
    c: PointOnObject(g42,g12)
    c: PointOnObject(g42,g-3)
    c: PointOnObject(g43,g9)
    c: PointOnObject(g43,g-7)
    c: Equal(g43,g42)
    c: Perpendicular(g-7,g43)
    c: Perpendicular(g9,g43)
    c: Perpendicular(g-3,g42)
    c: Perpendicular(g12,g42)
    c: PointOnObject(g44,g16)
    c: PointOnObject(g44,g-8)
    c: PointOnObject(g45,g-10)
    c: Equal(g45,g44)
    c: Perpendicular(g-8,g44)
    c: Perpendicular(g16,g44)
    c: PointOnObject(g45,g17)
    c: Perpendicular(g17,g45)
    c: Perpendicular(g-10,g45)
    c: PointOnObject(g46,g24)
    c: PointOnObject(g46,g-12)
    c: PointOnObject(g47,g-14)
    c: PointOnObject(g47,g25)
    c: Equal(g46,g47)
    c: Perpendicular(g-14,g47)
    c: Perpendicular(g25,g47)
    c: Perpendicular(g24,g46)
    c: Perpendicular(g-12,g46)
    c: Distance(g43) = 6.35
FEATURE [PartDesign::Pocket] Pocket009
  BaseFeature = -> Pocket008
  Direction = (0,-1,-2e-16)
  Length = 5.08
  Length2 = 5.08
  Profile = -> Sketch020
  ReferenceAxis = -> Sketch020 [N_Axis]
  Type = 1
FEATURE [Sketcher::SketchObject] Sketch021
  ExternalGeometry = -> [Pocket009]
  FullyConstrained = true
  MapMode = 5
  Placement = pos=(0,-3.302,-7e-16) rot=(1,0,0;1.5708rad)
  Support = -> [Pocket009]
  sketch-geometry (5):
    g0: LineSegment StartX=15.0855 StartY=0.453278 StartZ=0 EndX=15.0855 EndY=-16.0567 EndZ=0
    g1: LineSegment StartX=-17.7449 StartY=-13.5537 StartZ=0 EndX=17.0135 EndY=-13.5537 EndZ=0
    g2: LineSegment StartX=17.0135 StartY=-13.5537 StartZ=0 EndX=17.0135 EndY=-16.0567 EndZ=0
    g3: LineSegment StartX=17.0135 StartY=-16.0567 StartZ=0 EndX=-17.7449 EndY=-16.0567 EndZ=0
    g4: LineSegment StartX=-17.7449 StartY=-16.0567 StartZ=0 EndX=-17.7449 EndY=-13.5537 EndZ=0
  constraints (14):
    c: Coincident(g0,g-4)
    c: Vertical(g0)
    c: DistanceY(g0,g0) = 16.51
    c: Coincident(g1,g2)
    c: Coincident(g2,g3)
    c: Coincident(g3,g4)
    c: Coincident(g4,g1)
    c: Horizontal(g1)
    c: Horizontal(g3)
    c: Vertical(g2)
    c: Vertical(g4)
    c: Coincident(g1,g-3)
    c: PointOnObject(g-3,g2)
    c: PointOnObject(g0,g3)
FEATURE [PartDesign::Pocket] Pocket010
  BaseFeature = -> Pocket009
  Direction = (0,1,2e-16)
  Length = 5.08
  Length2 = 5.08
  Profile = -> Sketch021
  ReferenceAxis = -> Sketch021 [N_Axis]
  Type = 1
FEATURE [Sketcher::SketchObject] Sketch022
  ExternalGeometry = -> [Pocket010]
  FullyConstrained = true
  MapMode = 5
  Placement = pos=(0,-3.302,-7e-16) rot=(1,0,0;1.5708rad)
  Support = -> [Pocket010]
  sketch-geometry (60):
    g0: LineSegment StartX=-24.9437 StartY=123.343 StartZ=0 EndX=-10.6155 EndY=133.376 EndZ=0
    g1: LineSegment StartX=90.279 StartY=8.12025 StartZ=0 EndX=100.312 EndY=22.4485 EndZ=0
    g2: LineSegment StartX=-7.41018 StartY=-57.7308 StartZ=0 EndX=7.55535 EndY=-60.3696 EndZ=0
    g3: ArcOfCircle CenterX=-96.3222 CenterY=120.318 CenterZ=0 NormalX=0 NormalY=0 NormalZ=1 AngleXU=0 Radius=66.3082 StartAngle=4.90851 EndAngle=6.18966
    g4: ArcOfCircle CenterX=87.2543 CenterY=-63.2582 CenterZ=0 NormalX=0 NormalY=0 NormalZ=1 AngleXU=0 Radius=66.3082 StartAngle=1.66432 EndAngle=2.94548
    g5: ArcOfCircle CenterX=-95.0597 CenterY=-61.9958 CenterZ=0 NormalX=0 NormalY=0 NormalZ=1 AngleXU=0 Radius=78.7068 StartAngle=0.184534 EndAngle=1.38626
    g6: ArcOfCircle CenterX=210.915 CenterY=243.979 CenterZ=0 NormalX=0 NormalY=0 NormalZ=1 AngleXU=0 Radius=233.357 StartAngle=3.65573 EndAngle=4.19825
    g7: ArcOfCircle CenterX=-17.6593 CenterY=112.94 CenterZ=0 NormalX=0 NormalY=0 NormalZ=1 AngleXU=0 Radius=12.7 StartAngle=2.18166 EndAngle=3.04807
    g8: ArcOfCircle CenterX=-3.33106 CenterY=122.972 CenterZ=0 NormalX=0 NormalY=0 NormalZ=1 AngleXU=0 Radius=12.7 StartAngle=0.514136 EndAngle=2.18166
    g9: ArcOfCircle CenterX=89.9085 CenterY=29.7329 CenterZ=0 NormalX=0 NormalY=0 NormalZ=1 AngleXU=0 Radius=12.7 StartAngle=5.67232 EndAngle=7.33985
    g10: ArcOfCircle CenterX=79.8757 CenterY=15.4047 CenterZ=0 NormalX=0 NormalY=0 NormalZ=1 AngleXU=0 Radius=12.7 StartAngle=4.80592 EndAngle=5.67232
    g11: ArcOfCircle CenterX=9.76068 CenterY=-47.8625 CenterZ=0 NormalX=0 NormalY=0 NormalZ=1 AngleXU=0 Radius=12.7 StartAngle=4.53786 EndAngle=6.08707
    g12: ArcOfCircle CenterX=-5.20484 CenterY=-45.2237 CenterZ=0 NormalX=0 NormalY=0 NormalZ=1 AngleXU=0 Radius=12.7 StartAngle=3.32613 EndAngle=4.53786
    g13: LineSegment StartX=-90.7947 StartY=25.6538 StartZ=0 EndX=-93.4336 EndY=40.6193 EndZ=0
    g14: ArcOfCircle CenterX=-80.9265 CenterY=42.8246 CenterZ=0 NormalX=0 NormalY=0 NormalZ=1 AngleXU=0 Radius=12.7 StartAngle=1.76691 EndAngle=3.31613
    g15: ArcOfCircle CenterX=-78.2877 CenterY=27.8591 CenterZ=0 NormalX=0 NormalY=0 NormalZ=1 AngleXU=0 Radius=12.7 StartAngle=3.31613 EndAngle=4.52786
    g16: ArcOfCircle CenterX=-75.8664 CenterY=23.1055 CenterZ=0 NormalX=0 NormalY=0 NormalZ=1 AngleXU=0 Radius=3.175 StartAngle=3.31613 EndAngle=6.45772
    g17: ArcOfCircle CenterX=-80.277 CenterY=48.1197 CenterZ=0 NormalX=0 NormalY=0 NormalZ=1 AngleXU=0 Radius=3.175 StartAngle=0.174533 EndAngle=3.31613
    g18: LineSegment StartX=-72.7396 StartY=23.6569 StartZ=0 EndX=-77.1503 EndY=48.671 EndZ=0
    g19: LineSegment StartX=-83.4038 StartY=47.5683 StartZ=0 EndX=-78.9931 EndY=22.5542 EndZ=0
    g20: ArcOfCircle CenterX=-63.3593 CenterY=25.3109 CenterZ=0 NormalX=0 NormalY=0 NormalZ=1 AngleXU=0 Radius=3.175 StartAngle=3.31613 EndAngle=6.45772
    g21: ArcOfCircle CenterX=-67.77 CenterY=50.325 CenterZ=0 NormalX=0 NormalY=0 NormalZ=1 AngleXU=0 Radius=3.175 StartAngle=0.174533 EndAngle=3.31613
    g22: LineSegment StartX=-60.2325 StartY=25.8622 StartZ=0 EndX=-64.6432 EndY=50.8763 EndZ=0
    g23: LineSegment StartX=-70.8967 StartY=49.7737 StartZ=0 EndX=-66.4861 EndY=24.7595 EndZ=0
    g24: ArcOfCircle CenterX=-21.4323 CenterY=108.395 CenterZ=0 NormalX=0 NormalY=0 NormalZ=1 AngleXU=0 Radius=3.175 StartAngle=2.18166 EndAngle=5.32325
    g25: ArcOfCircle CenterX=-0.625811 CenterY=122.963 CenterZ=0 NormalX=0 NormalY=0 NormalZ=1 AngleXU=0 Radius=3.175 StartAngle=5.32325 EndAngle=8.46485
    g26: LineSegment StartX=-19.6112 StartY=105.794 StartZ=0 EndX=1.19529 EndY=120.363 EndZ=0
    g27: LineSegment StartX=-2.44692 StartY=125.564 StartZ=0 EndX=-23.2534 EndY=110.995 EndZ=0
    g28: ArcOfCircle CenterX=-14.1479 CenterY=97.9913 CenterZ=0 NormalX=0 NormalY=0 NormalZ=1 AngleXU=0 Radius=3.175 StartAngle=2.18166 EndAngle=5.32325
    g29: ArcOfCircle CenterX=6.65861 CenterY=112.56 CenterZ=0 NormalX=0 NormalY=0 NormalZ=1 AngleXU=0 Radius=3.175 StartAngle=5.32325 EndAngle=8.46485
    g30: LineSegment StartX=-12.3267 StartY=95.3905 StartZ=0 EndX=8.47972 EndY=109.959 EndZ=0
    g31: LineSegment StartX=4.83751 StartY=115.161 StartZ=0 EndX=-15.969 EndY=100.592 EndZ=0
    g32: ArcOfCircle CenterX=79.4962 CenterY=39.7226 CenterZ=0 NormalX=0 NormalY=0 NormalZ=1 AngleXU=0 Radius=3.175 StartAngle=5.67232 EndAngle=8.81391
    g33: ArcOfCircle CenterX=64.9273 CenterY=18.9161 CenterZ=0 NormalX=0 NormalY=0 NormalZ=1 AngleXU=0 Radius=3.175 StartAngle=2.53073 EndAngle=5.67232
    g34: LineSegment StartX=76.8954 StartY=41.5437 StartZ=0 EndX=62.3265 EndY=20.7372 EndZ=0
    g35: LineSegment StartX=67.5282 StartY=17.095 StartZ=0 EndX=82.097 EndY=37.9015 EndZ=0
    g36: ArcOfCircle CenterX=75.3306 CenterY=11.6317 CenterZ=0 NormalX=0 NormalY=0 NormalZ=1 AngleXU=0 Radius=3.175 StartAngle=2.53073 EndAngle=5.67232
    g37: ArcOfCircle CenterX=89.8994 CenterY=32.4381 CenterZ=0 NormalX=0 NormalY=0 NormalZ=1 AngleXU=0 Radius=3.175 StartAngle=5.67232 EndAngle=8.81391
    g38: LineSegment StartX=77.9314 StartY=9.81057 StartZ=0 EndX=92.5002 EndY=30.617 EndZ=0
    g39: LineSegment StartX=87.2986 StartY=34.2592 StartZ=0 EndX=72.7298 EndY=13.4528 EndZ=0
    g40: ArcOfCircle CenterX=-7.75308 CenterY=-30.2953 CenterZ=0 NormalX=0 NormalY=0 NormalZ=1 AngleXU=0 Radius=3.175 StartAngle=1.39626 EndAngle=4.53786
    g41: ArcOfCircle CenterX=17.261 CenterY=-34.706 CenterZ=0 NormalX=0 NormalY=0 NormalZ=1 AngleXU=0 Radius=3.175 StartAngle=4.53786 EndAngle=7.67945
    g42: LineSegment StartX=-8.30441 StartY=-33.4221 StartZ=0 EndX=16.7097 EndY=-37.8328 EndZ=0
    g43: LineSegment StartX=17.8124 StartY=-31.5792 StartZ=0 EndX=-7.20174 EndY=-27.1686 EndZ=0
    g44: ArcOfCircle CenterX=-9.95841 CenterY=-42.8024 CenterZ=0 NormalX=0 NormalY=0 NormalZ=1 AngleXU=0 Radius=3.175 StartAngle=1.39626 EndAngle=4.53786
    g45: ArcOfCircle CenterX=15.0557 CenterY=-47.2131 CenterZ=0 NormalX=0 NormalY=0 NormalZ=1 AngleXU=0 Radius=3.175 StartAngle=4.53786 EndAngle=7.67945
    g46: LineSegment StartX=-10.5097 StartY=-45.9292 StartZ=0 EndX=14.5044 EndY=-50.3398 EndZ=0
    g47: LineSegment StartX=15.607 StartY=-44.0863 StartZ=0 EndX=-9.40708 EndY=-39.6756 EndZ=0
    g48: LineSegment StartX=-9.52073 StartY=63.9533 StartZ=0 EndX=9.52927 EndY=63.9533 EndZ=0
    g49: LineSegment StartX=9.52927 StartY=63.9533 StartZ=0 EndX=9.52927 EndY=76.6533 EndZ=0
    g50: LineSegment StartX=9.52927 StartY=76.6533 StartZ=0 EndX=-9.52073 EndY=76.6533 EndZ=0
    g51: LineSegment StartX=-9.52073 StartY=76.6533 StartZ=0 EndX=-9.52073 EndY=63.9533 EndZ=0
    g52: LineSegment StartX=16.3555 StartY=26.67 StartZ=0 EndX=16.3555 EndY=0.533978 EndZ=0
    g53: LineSegment StartX=16.3555 StartY=0.533978 StartZ=0 EndX=17.0135 EndY=0.533978 EndZ=0
    g54: LineSegment StartX=17.0135 StartY=0.533978 StartZ=0 EndX=17.0135 EndY=-16.0567 EndZ=0
    g55: LineSegment StartX=17.0135 StartY=-16.0567 StartZ=0 EndX=-17.7449 EndY=-16.0567 EndZ=0
    g56: LineSegment StartX=-17.7449 StartY=-16.0567 StartZ=0 EndX=-17.7449 EndY=0.533978 EndZ=0
    g57: LineSegment StartX=-17.7449 StartY=0.533978 StartZ=0 EndX=-16.347 EndY=0.533978 EndZ=0
    g58: LineSegment StartX=-16.347 StartY=0.533978 StartZ=0 EndX=-16.347 EndY=26.67 EndZ=0
    g59: LineSegment StartX=-16.347 StartY=26.67 StartZ=0 EndX=16.3555 EndY=26.67 EndZ=0
  constraints (139):
    c: Coincident(g0,g-5)
    c: Coincident(g0,g-6)
    c: Coincident(g1,g-10)
    c: Coincident(g1,g-9)
    c: Coincident(g2,g-14)
    c: Coincident(g2,g-13)
    c: Coincident(g3,g-3)
    c: Coincident(g4,g-11)
    c: Coincident(g5,g-15)
    c: Coincident(g6,g-7)
    c: Coincident(g3,g-4)
    c: Coincident(g3,g-18)
    c: Coincident(g6,g-8)
    c: Coincident(g6,g-6)
    c: Coincident(g4,g-12)
    c: Coincident(g4,g-10)
    c: Coincident(g5,g-16)
    c: Coincident(g5,g-14)
    c: Coincident(g7,g-4)
    c: Coincident(g8,g-6)
    c: Coincident(g9,g-8)
    c: Coincident(g10,g-10)
    c: Coincident(g11,g-12)
    c: PointOnObject(g4,g11)
    c: Coincident(g7,g3)
    c: Coincident(g8,g6)
    c: PointOnObject(g8,g0)
    c: Coincident(g7,g0)
    c: Coincident(g9,g6)
    c: Coincident(g10,g-11)
    c: Block(g8)
    c: Block(g9)
    c: Block(g10)
    c: Coincident(g11,g-11)
    c: Coincident(g11,g2)
    c: Coincident(g12,g-14)
    c: PointOnObject(g2,g12)
    c: Coincident(g12,g-13)
    c: Coincident(g12,g5)
    c: Coincident(g13,g-18)
    c: Coincident(g13,g-17)
    c: Coincident(g14,g-18)
    c: Coincident(g14,g13)
    c: Coincident(g14,g3)
    c: Coincident(g15,g-16)
    c: Coincident(g15,g5)
    c: Coincident(g15,g13)
    c: Tangent(g16,g18) = -1.5708
    c: Tangent(g18,g17) = -1.5708
    c: Tangent(g17,g19) = -1.5708
    c: Tangent(g19,g16) = -1.5708
    c: Equal(g16,g17)
    c: Coincident(g16,g-25)
    c: Coincident(g17,g-24)
    c: Equal(g17,g-24)
    c: Tangent(g20,g22) = -1.5708
    c: Tangent(g22,g21) = -1.5708
    c: Tangent(g21,g23) = -1.5708
    c: Tangent(g23,g20) = -1.5708
    c: Equal(g20,g21)
    c: Coincident(g20,g-26)
    c: Coincident(g21,g-35)
    c: Equal(g21,g-35)
    c: Tangent(g24,g26) = -1.5708
    c: Tangent(g26,g25) = -1.5708
    c: Tangent(g25,g27) = -1.5708
    c: Tangent(g27,g24) = -1.5708
    c: Equal(g24,g25)
    c: Coincident(g24,g-21)
    c: Coincident(g25,g-20)
    c: Equal(g25,g-20)
    c: Tangent(g28,g30) = -1.5708
    c: Tangent(g30,g29) = -1.5708
    c: Tangent(g29,g31) = -1.5708
    c: Tangent(g31,g28) = -1.5708
    c: Equal(g28,g29)
    c: Coincident(g28,g-22)
    c: Coincident(g29,g-23)
    c: Equal(g29,g-23)
    c: Tangent(g32,g34) = -1.5708
    c: Tangent(g34,g33) = -1.5708
    c: Tangent(g33,g35) = -1.5708
    c: Tangent(g35,g32) = -1.5708
    c: Equal(g32,g33)
    c: Coincident(g32,g-28)
    c: Coincident(g33,g-27)
    c: Tangent(g36,g38) = -1.5708
    c: Tangent(g38,g37) = -1.5708
    c: Tangent(g37,g39) = -1.5708
    c: Tangent(g39,g36) = -1.5708
    c: Equal(g36,g37)
    c: Coincident(g36,g-29)
    c: Coincident(g37,g-30)
    c: Equal(g37,g-30)
    c: Equal(g32,g-28)
    c: Tangent(g40,g42) = -1.5708
    c: Tangent(g42,g41) = -1.5708
    c: Tangent(g41,g43) = -1.5708
    c: Tangent(g43,g40) = -1.5708
    c: Equal(g40,g41)
    c: Coincident(g40,g-32)
    c: Coincident(g41,g-31)
    c: Tangent(g44,g46) = -1.5708
    c: Tangent(g46,g45) = -1.5708
    c: Tangent(g45,g47) = -1.5708
    c: Tangent(g47,g44) = -1.5708
    c: Equal(g44,g45)
    c: Coincident(g44,g-34)
    c: Coincident(g45,g-33)
    c: Equal(g45,g-33)
    c: Equal(g41,g-31)
    c: Coincident(g48,g49)
    c: Coincident(g49,g50)
    c: Coincident(g50,g51)
    c: Coincident(g51,g48)
    c: Horizontal(g48)
    c: Horizontal(g50)
    c: Vertical(g49)
    c: Vertical(g51)
    c: Coincident(g48,g-39)
    c: Coincident(g49,g-37)
    c: Coincident(g-43,g52)
    c: Coincident(g52,g-43)
    c: Coincident(g52,g53)
    c: PointOnObject(g53,g-45)
    c: Horizontal(g53)
    c: Coincident(g53,g54)
    c: Coincident(g54,g-40)
    c: Coincident(g54,g55)
    c: Coincident(g55,g-40)
    c: Coincident(g55,g56)
    c: PointOnObject(g56,g-44)
    c: Coincident(g56,g57)
    c: Coincident(g57,g-42)
    c: Coincident(g57,g58)
    c: Coincident(g58,g-42)
    c: Coincident(g58,g59)
    c: Coincident(g59,g52)
    c: Horizontal(g57)
FEATURE [PartDesign::Pad] Pad005
  BaseFeature = -> Pocket010
  Direction = (0,-1,-2e-16)
  Length = 9.906
  Length2 = 9.906
  Profile = -> Sketch022
  ReferenceAxis = -> Sketch022 [N_Axis]
  Type = 3
  UpToFace = -> Pocket010 [Face68]
FEATURE [PartDesign::Fillet] Fillet001
  Base = -> Pad005 [Edge141,Edge145,Edge169,Edge175,Edge179,Edge183,Edge137,Edge133,Edge121]
  BaseFeature = -> Pad005
  Radius = 1.524
  SupportTransform = false
  UseAllEdges = false
FEATURE [PartDesign::Fillet] Fillet002
  Base = -> Fillet001 [Edge248,Edge247,Edge246,Edge245]
  BaseFeature = -> Fillet001
  Radius = 1.016
  SupportTransform = false
  UseAllEdges = false
FEATURE [PartDesign::Body] Body
  Group = -> [Sketch,Pad,Sketch001,DatumPlane,Sketch002,Pocket,Sketch003,Sketch004,Pocket001,Sketch005,Pocket002,Sketch006,Pocket003,Sketch007,Pocket004,Chamfer,DatumPlane001,Sketch008,Pad001,Fillet,Sketch009,Pad002,Sketch010,Pad003,Sketch011,Sketch012,SubtractiveLoft,Sketch013,Pocket005,Sketch014,Sketch015,SubtractiveLoft001,Sketch016,Pocket006,Sketch017,Pocket007,Sketch018,Pad004,Sketch019,Pocket008,+8 more]
  Origin = -> Origin
  Tip = -> Fillet002
